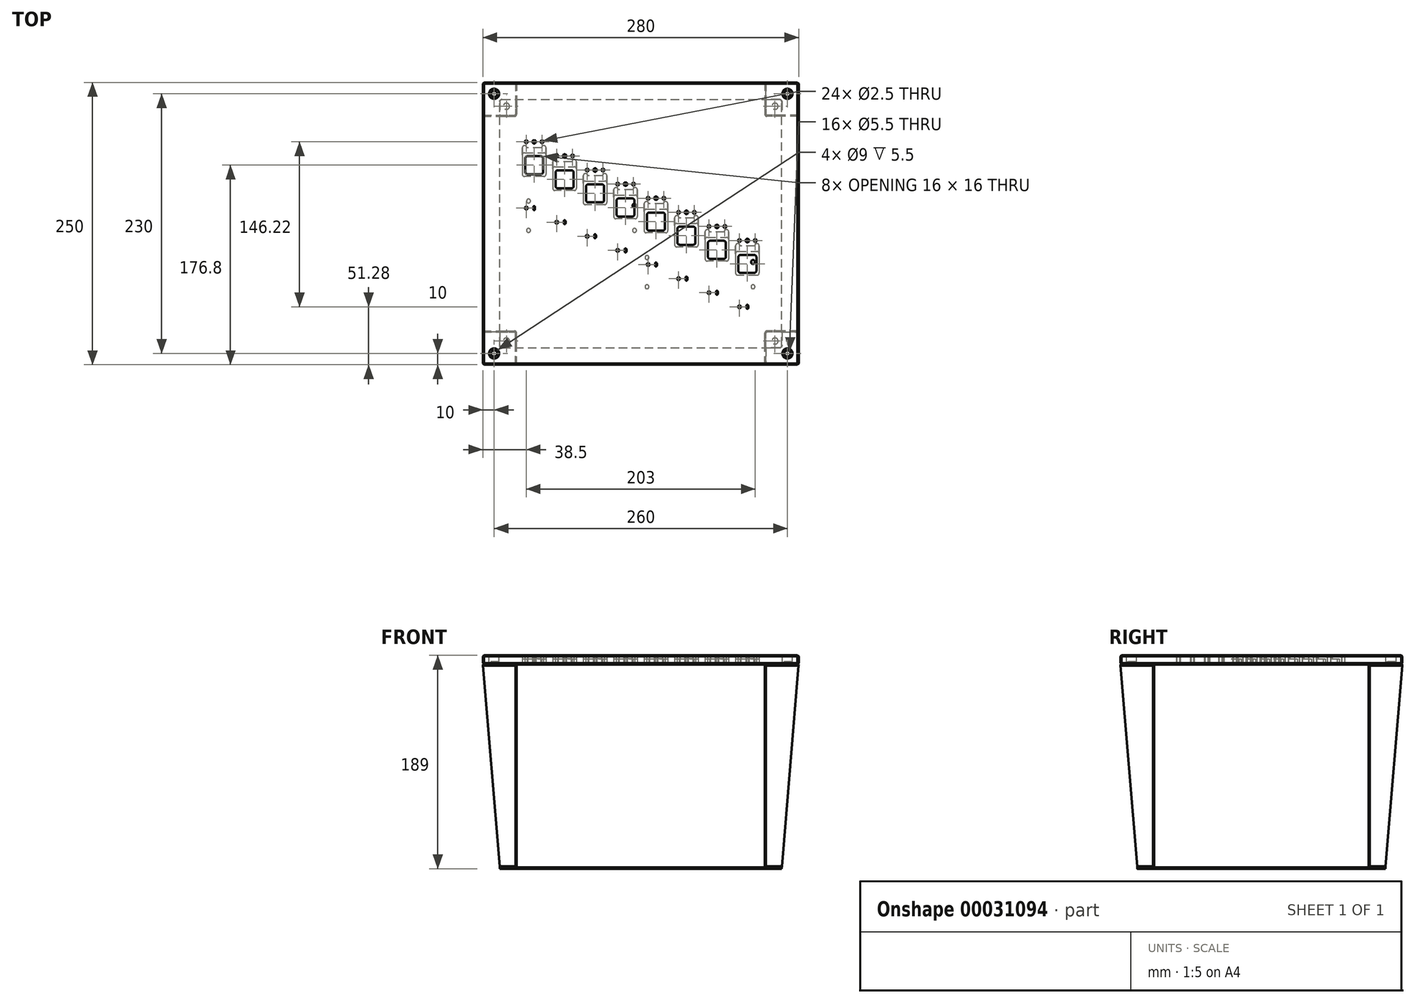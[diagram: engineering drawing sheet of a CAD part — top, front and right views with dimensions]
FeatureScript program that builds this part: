
annotation { "Feature Type Name" : "Feature", "Feature Type Description" : "" }
export const myFeature = defineFeature(function(context is Context, id is Id, definition is map)
    precondition{}
    {
        {
            var Q0;
            Q0=qCreatedBy(makeId("Top.planeOp"),FACE);
            var sketch = newSketch(context, id + "F0", { "sketchPlane" : qUnion([Q0])});
            skLineSegment(sketch, "E0", {"start": v(-94.5, 72.5) * mm, "end": v(-67.5, 60) * mm, "construction": true});
            skLineSegment(sketch, "E1", {"start": v(-67.5, 60) * mm, "end": v(-40.5, 47.5) * mm, "construction": true});
            skLineSegment(sketch, "E2", {"start": v(-40.5, 47.5) * mm, "end": v(-13.5, 35) * mm, "construction": true});
            skLineSegment(sketch, "E3", {"start": v(-13.5, 35) * mm, "end": v(13.5, 22.5) * mm, "construction": true});
            skLineSegment(sketch, "E4", {"start": v(13.5, 22.5) * mm, "end": v(40.5, 10) * mm, "construction": true});
            skLineSegment(sketch, "E5", {"start": v(40.5, 10) * mm, "end": v(67.5, -2.5) * mm, "construction": true});
            skLineSegment(sketch, "E6", {"start": v(67.5, -2.5) * mm, "end": v(94.5, -15) * mm, "construction": true});
            skLineSegment(sketch, "E7", {"start": v(-125, -110) * mm, "end": v(125, 110) * mm, "construction": true});
            skPoint(sketch, "E8", {"position": v(-125, 110) * mm});
            skPoint(sketch, "E9", {"position": v(125, 110) * mm});
            skPoint(sketch, "E10", {"position": v(125, -110) * mm});
            skPoint(sketch, "E11", {"position": v(-125, -110) * mm});
            skLineSegment(sketch, "E12", {"start": v(-125, 110) * mm, "end": v(125, 110) * mm, "construction": true});
            skLineSegment(sketch, "E13", {"start": v(125, 110) * mm, "end": v(125, -110) * mm, "construction": true});
            skLineSegment(sketch, "E14", {"start": v(125, -110) * mm, "end": v(-125, -110) * mm, "construction": true});
            skLineSegment(sketch, "E15", {"start": v(-125, -110) * mm, "end": v(-125, 110) * mm, "construction": true});
            skLineSegment(sketch, "E16", {"start": v(-94.5, 72.5) * mm, "end": v(-125, 72.5) * mm, "construction": true});
            skLineSegment(sketch, "E17", {"start": v(94.5, -15) * mm, "end": v(125, -15) * mm, "construction": true});
            skLineSegment(sketch, "E18", {"start": v(-94.5, 72.5) * mm, "end": v(-94.5, 110) * mm, "construction": true});
            skLineSegment(sketch, "E19", {"start": v(94.5, -15) * mm, "end": v(94.5, -110) * mm, "construction": true});
            skLineSegment(sketch, "E20.bottom", {"start": v(-140, 125) * mm, "end": v(140, 125) * mm});
            skLineSegment(sketch, "E20.top", {"start": v(-140, -125) * mm, "end": v(140, -125) * mm});
            skLineSegment(sketch, "E20.left", {"start": v(-140, 125) * mm, "end": v(-140, -125) * mm});
            skLineSegment(sketch, "E20.right", {"start": v(140, 125) * mm, "end": v(140, -125) * mm});
            skLineSegment(sketch, "E21", {"start": v(-47.5, 47.5) * mm, "end": v(-33.5, 47.5) * mm, "construction": true});
            skLineSegment(sketch, "E22", {"start": v(-40.5, 47.5) * mm, "end": v(-40.5, -11.22) * mm, "construction": true});
            skLineSegment(sketch, "E23", {"start": v(-40.5, -11.22) * mm, "end": v(-47.5, -11.22) * mm, "construction": true});
            skLineSegment(sketch, "E24.bottom", {"start": v(-46.5, 34.8) * mm, "end": v(-34.5, 34.8) * mm});
            skLineSegment(sketch, "E24.top", {"start": v(-46.5, 18.8) * mm, "end": v(-34.5, 18.8) * mm});
            skLineSegment(sketch, "E24.left", {"start": v(-48.5, 32.8) * mm, "end": v(-48.5, 20.8) * mm});
            skLineSegment(sketch, "E24.right", {"start": v(-32.5, 32.8) * mm, "end": v(-32.5, 20.8) * mm});
            skPoint(sketch, "E25.visualSharp", {"position": v(-48.5, 34.8) * mm});
            skArc(sketch, "E25.filletArc", {"start": v(-46.5, 34.8) * mm, "mid": v(-47.91, 34.21) * mm, "end": v(-48.5, 32.8) * mm});
            skPoint(sketch, "E26.visualSharp", {"position": v(-48.5, 18.8) * mm});
            skArc(sketch, "E26.filletArc", {"start": v(-48.5, 20.8) * mm, "mid": v(-47.91, 19.39) * mm, "end": v(-46.5, 18.8) * mm});
            skPoint(sketch, "E27.visualSharp", {"position": v(-32.5, 18.8) * mm});
            skArc(sketch, "E27.filletArc", {"start": v(-34.5, 18.8) * mm, "mid": v(-33.09, 19.39) * mm, "end": v(-32.5, 20.8) * mm});
            skPoint(sketch, "E28.visualSharp", {"position": v(-32.5, 34.8) * mm});
            skArc(sketch, "E28.filletArc", {"start": v(-32.5, 32.8) * mm, "mid": v(-33.09, 34.21) * mm, "end": v(-34.5, 34.8) * mm});
            skPoint(sketch, "E29", {"position": v(-40.5, 34.8) * mm});
            skLineSegment(sketch, "E30", {"start": v(-40.5, -10.22) * mm, "end": v(-40.5, -12.22) * mm});
            skArc(sketch, "E31.0.startCap", {"start": v(-41.27, -10.22) * mm, "mid": v(-40.5, -9.45) * mm, "end": v(-39.73, -10.22) * mm});
            skArc(sketch, "E31.0.endCap", {"start": v(-39.73, -12.22) * mm, "mid": v(-40.5, -12.98) * mm, "end": v(-41.27, -12.22) * mm});
            skLineSegment(sketch, "E31.0.left", {"start": v(-39.73, -10.22) * mm, "end": v(-39.73, -12.22) * mm});
            skLineSegment(sketch, "E31.0.right", {"start": v(-41.26, -10.22) * mm, "end": v(-41.26, -12.22) * mm});
            skCircle(sketch, "E32", {"center": v(-40.5, 47.5) * mm, "radius": 1.52 * mm});
            skCircle(sketch, "E33", {"center": v(-47.5, 47.5) * mm, "radius": 1.25 * mm});
            skCircle(sketch, "E34", {"center": v(-33.5, 47.5) * mm, "radius": 1.25 * mm});
            skCircle(sketch, "E35", {"center": v(-47.5, -11.22) * mm, "radius": 1.25 * mm});
            skPoint(sketch, "E36.visualSharp", {"position": v(-75.5, 31.3) * mm});
            skPoint(sketch, "E37.visualSharp", {"position": v(-59.5, 47.3) * mm});
            skPoint(sketch, "E38.visualSharp", {"position": v(-75.5, 47.3) * mm});
            skPoint(sketch, "E39.visualSharp", {"position": v(-59.5, 31.3) * mm});
            skLineSegment(sketch, "E40", {"start": v(-67.5, 60) * mm, "end": v(-67.5, 1.28) * mm, "construction": true});
            skPoint(sketch, "E41", {"position": v(-67.5, 47.3) * mm});
            skCircle(sketch, "E42", {"center": v(-67.5, 60) * mm, "radius": 1.52 * mm});
            skCircle(sketch, "E43", {"center": v(-74.5, 60) * mm, "radius": 1.25 * mm});
            skCircle(sketch, "E44", {"center": v(-74.5, 1.28) * mm, "radius": 1.25 * mm});
            skLineSegment(sketch, "E45", {"start": v(-67.5, 1.28) * mm, "end": v(-74.5, 1.28) * mm, "construction": true});
            skLineSegment(sketch, "E46", {"start": v(-74.5, 60) * mm, "end": v(-60.5, 60) * mm, "construction": true});
            skLineSegment(sketch, "E47.top", {"start": v(-73.5, 31.3) * mm, "end": v(-61.5, 31.3) * mm});
            skLineSegment(sketch, "E47.right", {"start": v(-59.5, 45.3) * mm, "end": v(-59.5, 33.3) * mm});
            skArc(sketch, "E39.filletArc", {"start": v(-61.5, 31.3) * mm, "mid": v(-60.09, 31.89) * mm, "end": v(-59.5, 33.3) * mm});
            skArc(sketch, "E38.filletArc", {"start": v(-73.5, 47.3) * mm, "mid": v(-74.91, 46.71) * mm, "end": v(-75.5, 45.3) * mm});
            skLineSegment(sketch, "E47.left", {"start": v(-75.5, 45.3) * mm, "end": v(-75.5, 33.3) * mm});
            skArc(sketch, "E36.filletArc", {"start": v(-75.5, 33.3) * mm, "mid": v(-74.91, 31.89) * mm, "end": v(-73.5, 31.3) * mm});
            skArc(sketch, "E37.filletArc", {"start": v(-59.5, 45.3) * mm, "mid": v(-60.09, 46.71) * mm, "end": v(-61.5, 47.3) * mm});
            skLineSegment(sketch, "E47.bottom", {"start": v(-73.5, 47.3) * mm, "end": v(-61.5, 47.3) * mm});
            skCircle(sketch, "E48", {"center": v(-60.5, 60) * mm, "radius": 1.25 * mm});
            skArc(sketch, "E49.0.endCap", {"start": v(-66.73, 0.28) * mm, "mid": v(-67.5, -0.48) * mm, "end": v(-68.26, 0.28) * mm});
            skArc(sketch, "E49.0.startCap", {"start": v(-68.26, 2.28) * mm, "mid": v(-67.5, 3.05) * mm, "end": v(-66.73, 2.28) * mm});
            skLineSegment(sketch, "E49.0.right", {"start": v(-68.26, 2.28) * mm, "end": v(-68.26, 0.28) * mm});
            skLineSegment(sketch, "E49.0.left", {"start": v(-66.73, 2.28) * mm, "end": v(-66.73, 0.28) * mm});
            skLineSegment(sketch, "E50", {"start": v(-67.5, 2.28) * mm, "end": v(-67.5, 0.28) * mm});
            skPoint(sketch, "E51.visualSharp", {"position": v(-102.5, 43.8) * mm});
            skPoint(sketch, "E52.visualSharp", {"position": v(-86.5, 59.8) * mm});
            skPoint(sketch, "E53.visualSharp", {"position": v(-102.5, 59.8) * mm});
            skPoint(sketch, "E54.visualSharp", {"position": v(-86.5, 43.8) * mm});
            skLineSegment(sketch, "E55", {"start": v(-94.5, 72.5) * mm, "end": v(-94.5, 13.78) * mm, "construction": true});
            skPoint(sketch, "E56", {"position": v(-94.5, 59.8) * mm});
            skCircle(sketch, "E57", {"center": v(-94.5, 72.5) * mm, "radius": 1.52 * mm});
            skCircle(sketch, "E58", {"center": v(-101.5, 72.5) * mm, "radius": 1.25 * mm});
            skCircle(sketch, "E59", {"center": v(-101.5, 13.78) * mm, "radius": 1.25 * mm});
            skLineSegment(sketch, "E60", {"start": v(-94.5, 13.78) * mm, "end": v(-101.5, 13.78) * mm, "construction": true});
            skLineSegment(sketch, "E61", {"start": v(-101.5, 72.5) * mm, "end": v(-87.5, 72.5) * mm, "construction": true});
            skLineSegment(sketch, "E62.top", {"start": v(-100.5, 43.8) * mm, "end": v(-88.5, 43.8) * mm});
            skLineSegment(sketch, "E62.right", {"start": v(-86.5, 57.8) * mm, "end": v(-86.5, 45.8) * mm});
            skArc(sketch, "E54.filletArc", {"start": v(-88.5, 43.8) * mm, "mid": v(-87.09, 44.39) * mm, "end": v(-86.5, 45.8) * mm});
            skArc(sketch, "E53.filletArc", {"start": v(-100.5, 59.8) * mm, "mid": v(-101.91, 59.21) * mm, "end": v(-102.5, 57.8) * mm});
            skLineSegment(sketch, "E62.left", {"start": v(-102.5, 57.8) * mm, "end": v(-102.5, 45.8) * mm});
            skArc(sketch, "E51.filletArc", {"start": v(-102.5, 45.8) * mm, "mid": v(-101.91, 44.39) * mm, "end": v(-100.5, 43.8) * mm});
            skArc(sketch, "E52.filletArc", {"start": v(-86.5, 57.8) * mm, "mid": v(-87.09, 59.21) * mm, "end": v(-88.5, 59.8) * mm});
            skLineSegment(sketch, "E62.bottom", {"start": v(-100.5, 59.8) * mm, "end": v(-88.5, 59.8) * mm});
            skCircle(sketch, "E63", {"center": v(-87.5, 72.5) * mm, "radius": 1.25 * mm});
            skArc(sketch, "E64.0.endCap", {"start": v(-93.73, 12.78) * mm, "mid": v(-94.5, 12.02) * mm, "end": v(-95.26, 12.78) * mm});
            skArc(sketch, "E64.0.startCap", {"start": v(-95.26, 14.78) * mm, "mid": v(-94.5, 15.55) * mm, "end": v(-93.73, 14.78) * mm});
            skLineSegment(sketch, "E64.0.right", {"start": v(-95.26, 14.78) * mm, "end": v(-95.26, 12.78) * mm});
            skLineSegment(sketch, "E64.0.left", {"start": v(-93.73, 14.78) * mm, "end": v(-93.73, 12.78) * mm});
            skLineSegment(sketch, "E65", {"start": v(-94.5, 14.78) * mm, "end": v(-94.5, 12.78) * mm});
            skPoint(sketch, "E66.visualSharp", {"position": v(-21.5, 6.3) * mm});
            skPoint(sketch, "E67.visualSharp", {"position": v(-5.5, 22.3) * mm});
            skPoint(sketch, "E68.visualSharp", {"position": v(-21.5, 22.3) * mm});
            skPoint(sketch, "E69.visualSharp", {"position": v(-5.5, 6.3) * mm});
            skLineSegment(sketch, "E70", {"start": v(-13.5, 35) * mm, "end": v(-13.5, -23.72) * mm, "construction": true});
            skPoint(sketch, "E71", {"position": v(-13.5, 22.3) * mm});
            skCircle(sketch, "E72", {"center": v(-13.5, 35) * mm, "radius": 1.52 * mm});
            skCircle(sketch, "E73", {"center": v(-20.5, 35) * mm, "radius": 1.25 * mm});
            skCircle(sketch, "E74", {"center": v(-20.5, -23.72) * mm, "radius": 1.25 * mm});
            skLineSegment(sketch, "E75", {"start": v(-13.5, -23.72) * mm, "end": v(-20.5, -23.72) * mm, "construction": true});
            skLineSegment(sketch, "E76", {"start": v(-20.5, 35) * mm, "end": v(-6.5, 35) * mm, "construction": true});
            skLineSegment(sketch, "E77.top", {"start": v(-19.5, 6.3) * mm, "end": v(-7.5, 6.3) * mm});
            skLineSegment(sketch, "E77.right", {"start": v(-5.5, 20.3) * mm, "end": v(-5.5, 8.3) * mm});
            skArc(sketch, "E69.filletArc", {"start": v(-7.5, 6.3) * mm, "mid": v(-6.09, 6.89) * mm, "end": v(-5.5, 8.3) * mm});
            skArc(sketch, "E68.filletArc", {"start": v(-19.5, 22.3) * mm, "mid": v(-20.91, 21.71) * mm, "end": v(-21.5, 20.3) * mm});
            skLineSegment(sketch, "E77.left", {"start": v(-21.5, 20.3) * mm, "end": v(-21.5, 8.3) * mm});
            skArc(sketch, "E66.filletArc", {"start": v(-21.5, 8.3) * mm, "mid": v(-20.91, 6.89) * mm, "end": v(-19.5, 6.3) * mm});
            skArc(sketch, "E67.filletArc", {"start": v(-5.5, 20.3) * mm, "mid": v(-6.09, 21.71) * mm, "end": v(-7.5, 22.3) * mm});
            skLineSegment(sketch, "E77.bottom", {"start": v(-19.5, 22.3) * mm, "end": v(-7.5, 22.3) * mm});
            skCircle(sketch, "E78", {"center": v(-6.5, 35) * mm, "radius": 1.25 * mm});
            skArc(sketch, "E79.0.endCap", {"start": v(-12.73, -24.72) * mm, "mid": v(-13.5, -25.48) * mm, "end": v(-14.27, -24.72) * mm});
            skArc(sketch, "E79.0.startCap", {"start": v(-14.27, -22.72) * mm, "mid": v(-13.5, -21.95) * mm, "end": v(-12.73, -22.72) * mm});
            skLineSegment(sketch, "E79.0.right", {"start": v(-14.26, -22.72) * mm, "end": v(-14.26, -24.72) * mm});
            skLineSegment(sketch, "E79.0.left", {"start": v(-12.73, -22.72) * mm, "end": v(-12.73, -24.72) * mm});
            skLineSegment(sketch, "E80", {"start": v(-13.5, -22.72) * mm, "end": v(-13.5, -24.72) * mm});
            skPoint(sketch, "E81.visualSharp", {"position": v(5.5, -6.2) * mm});
            skPoint(sketch, "E82.visualSharp", {"position": v(21.5, 9.8) * mm});
            skPoint(sketch, "E83.visualSharp", {"position": v(5.5, 9.8) * mm});
            skPoint(sketch, "E84.visualSharp", {"position": v(21.5, -6.2) * mm});
            skLineSegment(sketch, "E85", {"start": v(13.5, 22.5) * mm, "end": v(13.5, -36.22) * mm, "construction": true});
            skPoint(sketch, "E86", {"position": v(13.5, 9.8) * mm});
            skCircle(sketch, "E87", {"center": v(13.5, 22.5) * mm, "radius": 1.52 * mm});
            skCircle(sketch, "E88", {"center": v(6.5, 22.5) * mm, "radius": 1.25 * mm});
            skCircle(sketch, "E89", {"center": v(6.5, -36.22) * mm, "radius": 1.25 * mm});
            skLineSegment(sketch, "E90", {"start": v(13.5, -36.22) * mm, "end": v(6.5, -36.22) * mm, "construction": true});
            skLineSegment(sketch, "E91", {"start": v(6.5, 22.5) * mm, "end": v(20.5, 22.5) * mm, "construction": true});
            skLineSegment(sketch, "E92.top", {"start": v(7.5, -6.2) * mm, "end": v(19.5, -6.2) * mm});
            skLineSegment(sketch, "E92.right", {"start": v(21.5, 7.8) * mm, "end": v(21.5, -4.2) * mm});
            skArc(sketch, "E84.filletArc", {"start": v(19.5, -6.2) * mm, "mid": v(20.91, -5.61) * mm, "end": v(21.5, -4.2) * mm});
            skArc(sketch, "E83.filletArc", {"start": v(7.5, 9.8) * mm, "mid": v(6.09, 9.21) * mm, "end": v(5.5, 7.8) * mm});
            skLineSegment(sketch, "E92.left", {"start": v(5.5, 7.8) * mm, "end": v(5.5, -4.2) * mm});
            skArc(sketch, "E81.filletArc", {"start": v(5.5, -4.2) * mm, "mid": v(6.09, -5.61) * mm, "end": v(7.5, -6.2) * mm});
            skArc(sketch, "E82.filletArc", {"start": v(21.5, 7.8) * mm, "mid": v(20.91, 9.21) * mm, "end": v(19.5, 9.8) * mm});
            skLineSegment(sketch, "E92.bottom", {"start": v(7.5, 9.8) * mm, "end": v(19.5, 9.8) * mm});
            skCircle(sketch, "E93", {"center": v(20.5, 22.5) * mm, "radius": 1.25 * mm});
            skArc(sketch, "E94.0.endCap", {"start": v(14.27, -37.22) * mm, "mid": v(13.5, -37.98) * mm, "end": v(12.74, -37.22) * mm});
            skArc(sketch, "E94.0.startCap", {"start": v(12.74, -35.22) * mm, "mid": v(13.5, -34.45) * mm, "end": v(14.27, -35.22) * mm});
            skLineSegment(sketch, "E94.0.right", {"start": v(12.74, -35.22) * mm, "end": v(12.74, -37.22) * mm});
            skLineSegment(sketch, "E94.0.left", {"start": v(14.27, -35.22) * mm, "end": v(14.27, -37.22) * mm});
            skLineSegment(sketch, "E95", {"start": v(13.5, -35.22) * mm, "end": v(13.5, -37.22) * mm});
            skPoint(sketch, "E96.visualSharp", {"position": v(32.5, -18.7) * mm});
            skPoint(sketch, "E97.visualSharp", {"position": v(48.5, -2.7) * mm});
            skPoint(sketch, "E98.visualSharp", {"position": v(32.5, -2.7) * mm});
            skPoint(sketch, "E99.visualSharp", {"position": v(48.5, -18.7) * mm});
            skLineSegment(sketch, "E100", {"start": v(40.5, 10) * mm, "end": v(40.5, -48.72) * mm, "construction": true});
            skPoint(sketch, "E101", {"position": v(40.5, -2.7) * mm});
            skCircle(sketch, "E102", {"center": v(40.5, 10) * mm, "radius": 1.52 * mm});
            skCircle(sketch, "E103", {"center": v(33.5, 10) * mm, "radius": 1.25 * mm});
            skCircle(sketch, "E104", {"center": v(33.5, -48.72) * mm, "radius": 1.25 * mm});
            skLineSegment(sketch, "E105", {"start": v(40.5, -48.72) * mm, "end": v(33.5, -48.72) * mm, "construction": true});
            skLineSegment(sketch, "E106", {"start": v(33.5, 10) * mm, "end": v(47.5, 10) * mm, "construction": true});
            skLineSegment(sketch, "E107.top", {"start": v(34.5, -18.7) * mm, "end": v(46.5, -18.7) * mm});
            skLineSegment(sketch, "E107.right", {"start": v(48.5, -4.7) * mm, "end": v(48.5, -16.7) * mm});
            skArc(sketch, "E99.filletArc", {"start": v(46.5, -18.7) * mm, "mid": v(47.91, -18.11) * mm, "end": v(48.5, -16.7) * mm});
            skArc(sketch, "E98.filletArc", {"start": v(34.5, -2.7) * mm, "mid": v(33.09, -3.29) * mm, "end": v(32.5, -4.7) * mm});
            skLineSegment(sketch, "E107.left", {"start": v(32.5, -4.7) * mm, "end": v(32.5, -16.7) * mm});
            skArc(sketch, "E96.filletArc", {"start": v(32.5, -16.7) * mm, "mid": v(33.09, -18.11) * mm, "end": v(34.5, -18.7) * mm});
            skArc(sketch, "E97.filletArc", {"start": v(48.5, -4.7) * mm, "mid": v(47.91, -3.29) * mm, "end": v(46.5, -2.7) * mm});
            skLineSegment(sketch, "E107.bottom", {"start": v(34.5, -2.7) * mm, "end": v(46.5, -2.7) * mm});
            skCircle(sketch, "E108", {"center": v(47.5, 10) * mm, "radius": 1.25 * mm});
            skArc(sketch, "E109.0.endCap", {"start": v(41.27, -49.72) * mm, "mid": v(40.5, -50.48) * mm, "end": v(39.73, -49.72) * mm});
            skArc(sketch, "E109.0.startCap", {"start": v(39.73, -47.72) * mm, "mid": v(40.5, -46.95) * mm, "end": v(41.27, -47.72) * mm});
            skLineSegment(sketch, "E109.0.right", {"start": v(39.73, -47.72) * mm, "end": v(39.73, -49.72) * mm});
            skLineSegment(sketch, "E109.0.left", {"start": v(41.26, -47.72) * mm, "end": v(41.26, -49.72) * mm});
            skLineSegment(sketch, "E110", {"start": v(40.5, -47.72) * mm, "end": v(40.5, -49.72) * mm});
            skPoint(sketch, "E111.visualSharp", {"position": v(59.5, -31.2) * mm});
            skPoint(sketch, "E112.visualSharp", {"position": v(75.5, -15.2) * mm});
            skPoint(sketch, "E113.visualSharp", {"position": v(59.5, -15.2) * mm});
            skPoint(sketch, "E114.visualSharp", {"position": v(75.5, -31.2) * mm});
            skLineSegment(sketch, "E115", {"start": v(67.5, -2.5) * mm, "end": v(67.5, -61.22) * mm, "construction": true});
            skPoint(sketch, "E116", {"position": v(67.5, -15.2) * mm});
            skCircle(sketch, "E117", {"center": v(67.5, -2.5) * mm, "radius": 1.52 * mm});
            skCircle(sketch, "E118", {"center": v(60.5, -2.5) * mm, "radius": 1.25 * mm});
            skCircle(sketch, "E119", {"center": v(60.5, -61.22) * mm, "radius": 1.25 * mm});
            skLineSegment(sketch, "E120", {"start": v(67.5, -61.22) * mm, "end": v(60.5, -61.22) * mm, "construction": true});
            skLineSegment(sketch, "E121", {"start": v(60.5, -2.5) * mm, "end": v(74.5, -2.5) * mm, "construction": true});
            skLineSegment(sketch, "E122.top", {"start": v(61.5, -31.2) * mm, "end": v(73.5, -31.2) * mm});
            skLineSegment(sketch, "E122.right", {"start": v(75.5, -17.2) * mm, "end": v(75.5, -29.2) * mm});
            skArc(sketch, "E114.filletArc", {"start": v(73.5, -31.2) * mm, "mid": v(74.91, -30.61) * mm, "end": v(75.5, -29.2) * mm});
            skArc(sketch, "E113.filletArc", {"start": v(61.5, -15.2) * mm, "mid": v(60.09, -15.79) * mm, "end": v(59.5, -17.2) * mm});
            skLineSegment(sketch, "E122.left", {"start": v(59.5, -17.2) * mm, "end": v(59.5, -29.2) * mm});
            skArc(sketch, "E111.filletArc", {"start": v(59.5, -29.2) * mm, "mid": v(60.09, -30.61) * mm, "end": v(61.5, -31.2) * mm});
            skArc(sketch, "E112.filletArc", {"start": v(75.5, -17.2) * mm, "mid": v(74.91, -15.79) * mm, "end": v(73.5, -15.2) * mm});
            skLineSegment(sketch, "E122.bottom", {"start": v(61.5, -15.2) * mm, "end": v(73.5, -15.2) * mm});
            skCircle(sketch, "E123", {"center": v(74.5, -2.5) * mm, "radius": 1.25 * mm});
            skArc(sketch, "E124.0.endCap", {"start": v(68.26, -62.22) * mm, "mid": v(67.5, -62.98) * mm, "end": v(66.73, -62.22) * mm});
            skArc(sketch, "E124.0.startCap", {"start": v(66.73, -60.22) * mm, "mid": v(67.5, -59.45) * mm, "end": v(68.26, -60.22) * mm});
            skLineSegment(sketch, "E124.0.right", {"start": v(66.73, -60.22) * mm, "end": v(66.73, -62.22) * mm});
            skLineSegment(sketch, "E124.0.left", {"start": v(68.26, -60.22) * mm, "end": v(68.26, -62.22) * mm});
            skLineSegment(sketch, "E125", {"start": v(67.5, -60.22) * mm, "end": v(67.5, -62.22) * mm});
            skPoint(sketch, "E126.visualSharp", {"position": v(86.5, -43.7) * mm});
            skPoint(sketch, "E127.visualSharp", {"position": v(102.5, -27.7) * mm});
            skPoint(sketch, "E128.visualSharp", {"position": v(86.5, -27.7) * mm});
            skPoint(sketch, "E129.visualSharp", {"position": v(102.5, -43.7) * mm});
            skLineSegment(sketch, "E130", {"start": v(94.5, -15) * mm, "end": v(94.5, -73.72) * mm, "construction": true});
            skPoint(sketch, "E131", {"position": v(94.5, -27.7) * mm});
            skCircle(sketch, "E132", {"center": v(94.5, -15) * mm, "radius": 1.52 * mm});
            skCircle(sketch, "E133", {"center": v(87.5, -15) * mm, "radius": 1.25 * mm});
            skCircle(sketch, "E134", {"center": v(87.5, -73.72) * mm, "radius": 1.25 * mm});
            skLineSegment(sketch, "E135", {"start": v(94.5, -73.72) * mm, "end": v(87.5, -73.72) * mm, "construction": true});
            skLineSegment(sketch, "E136", {"start": v(87.5, -15) * mm, "end": v(101.5, -15) * mm, "construction": true});
            skLineSegment(sketch, "E137.top", {"start": v(88.5, -43.7) * mm, "end": v(100.5, -43.7) * mm});
            skLineSegment(sketch, "E137.right", {"start": v(102.5, -29.7) * mm, "end": v(102.5, -41.7) * mm});
            skArc(sketch, "E129.filletArc", {"start": v(100.5, -43.7) * mm, "mid": v(101.91, -43.11) * mm, "end": v(102.5, -41.7) * mm});
            skArc(sketch, "E128.filletArc", {"start": v(88.5, -27.7) * mm, "mid": v(87.09, -28.29) * mm, "end": v(86.5, -29.7) * mm});
            skLineSegment(sketch, "E137.left", {"start": v(86.5, -29.7) * mm, "end": v(86.5, -41.7) * mm});
            skArc(sketch, "E126.filletArc", {"start": v(86.5, -41.7) * mm, "mid": v(87.09, -43.11) * mm, "end": v(88.5, -43.7) * mm});
            skArc(sketch, "E127.filletArc", {"start": v(102.5, -29.7) * mm, "mid": v(101.91, -28.29) * mm, "end": v(100.5, -27.7) * mm});
            skLineSegment(sketch, "E137.bottom", {"start": v(88.5, -27.7) * mm, "end": v(100.5, -27.7) * mm});
            skCircle(sketch, "E138", {"center": v(101.5, -15) * mm, "radius": 1.25 * mm});
            skArc(sketch, "E139.0.endCap", {"start": v(95.27, -74.72) * mm, "mid": v(94.5, -75.49) * mm, "end": v(93.73, -74.72) * mm});
            skArc(sketch, "E139.0.startCap", {"start": v(93.73, -72.72) * mm, "mid": v(94.5, -71.96) * mm, "end": v(95.27, -72.72) * mm});
            skLineSegment(sketch, "E139.0.right", {"start": v(93.73, -72.72) * mm, "end": v(93.73, -74.72) * mm});
            skLineSegment(sketch, "E139.0.left", {"start": v(95.26, -72.72) * mm, "end": v(95.26, -74.72) * mm});
            skLineSegment(sketch, "E140", {"start": v(94.5, -72.72) * mm, "end": v(94.5, -74.72) * mm});
            skSolve(sketch);
        }
        {
            var Q0;
            Q0 = qSketchRegion(id + "F0", true);
            extrude(context, id + "F1", {"entities" : qUnion([Q0]), "depth" : 8 * mm});
        }
        {
            var Q0;
            Q0=makeQuery(id+"F1.opExtrude","CAP_FACE",FACE,{"disambiguationData":[OSD([sQuery(id+"F0.wireOp",EDGE,"E20.bottom"),sQuery(id+"F0.wireOp",EDGE,"E20.top"),sQuery(id+"F0.wireOp",EDGE,"E20.left"),sQuery(id+"F0.wireOp",EDGE,"E20.right"),sQuery(id+"F0.wireOp",EDGE,"E24.bottom"),sQuery(id+"F0.wireOp",EDGE,"E24.top"),sQuery(id+"F0.wireOp",EDGE,"E24.left"),sQuery(id+"F0.wireOp",EDGE,"E24.right"),sQuery(id+"F0.wireOp",EDGE,"E25.filletArc"),sQuery(id+"F0.wireOp",EDGE,"E26.filletArc"),sQuery(id+"F0.wireOp",EDGE,"E27.filletArc"),sQuery(id+"F0.wireOp",EDGE,"E28.filletArc"),sQuery(id+"F0.wireOp",EDGE,"E31.0.startCap"),sQuery(id+"F0.wireOp",EDGE,"E31.0.endCap"),sQuery(id+"F0.wireOp",EDGE,"E31.0.left"),sQuery(id+"F0.wireOp",EDGE,"E31.0.right"),sQuery(id+"F0.wireOp",EDGE,"E32"),sQuery(id+"F0.wireOp",EDGE,"E33"),sQuery(id+"F0.wireOp",EDGE,"E34"),sQuery(id+"F0.wireOp",EDGE,"E35"),sQuery(id+"F0.wireOp",EDGE,"E42"),sQuery(id+"F0.wireOp",EDGE,"E43"),sQuery(id+"F0.wireOp",EDGE,"E44"),sQuery(id+"F0.wireOp",EDGE,"E47.top"),sQuery(id+"F0.wireOp",EDGE,"E47.right"),sQuery(id+"F0.wireOp",EDGE,"E39.filletArc"),sQuery(id+"F0.wireOp",EDGE,"E38.filletArc"),sQuery(id+"F0.wireOp",EDGE,"E47.left"),sQuery(id+"F0.wireOp",EDGE,"E36.filletArc"),sQuery(id+"F0.wireOp",EDGE,"E37.filletArc"),sQuery(id+"F0.wireOp",EDGE,"E47.bottom"),sQuery(id+"F0.wireOp",EDGE,"E48"),sQuery(id+"F0.wireOp",EDGE,"E49.0.endCap"),sQuery(id+"F0.wireOp",EDGE,"E49.0.startCap"),sQuery(id+"F0.wireOp",EDGE,"E49.0.right"),sQuery(id+"F0.wireOp",EDGE,"E49.0.left"),sQuery(id+"F0.wireOp",EDGE,"E57"),sQuery(id+"F0.wireOp",EDGE,"E58"),sQuery(id+"F0.wireOp",EDGE,"E59"),sQuery(id+"F0.wireOp",EDGE,"E62.top"),sQuery(id+"F0.wireOp",EDGE,"E62.right"),sQuery(id+"F0.wireOp",EDGE,"E54.filletArc"),sQuery(id+"F0.wireOp",EDGE,"E53.filletArc"),sQuery(id+"F0.wireOp",EDGE,"E62.left"),sQuery(id+"F0.wireOp",EDGE,"E51.filletArc"),sQuery(id+"F0.wireOp",EDGE,"E52.filletArc"),sQuery(id+"F0.wireOp",EDGE,"E62.bottom"),sQuery(id+"F0.wireOp",EDGE,"E63"),sQuery(id+"F0.wireOp",EDGE,"E64.0.endCap"),sQuery(id+"F0.wireOp",EDGE,"E64.0.startCap"),sQuery(id+"F0.wireOp",EDGE,"E64.0.right"),sQuery(id+"F0.wireOp",EDGE,"E64.0.left"),sQuery(id+"F0.wireOp",EDGE,"E72"),sQuery(id+"F0.wireOp",EDGE,"E73"),sQuery(id+"F0.wireOp",EDGE,"E74"),sQuery(id+"F0.wireOp",EDGE,"E77.top"),sQuery(id+"F0.wireOp",EDGE,"E77.right"),sQuery(id+"F0.wireOp",EDGE,"E69.filletArc"),sQuery(id+"F0.wireOp",EDGE,"E68.filletArc"),sQuery(id+"F0.wireOp",EDGE,"E77.left"),sQuery(id+"F0.wireOp",EDGE,"E66.filletArc"),sQuery(id+"F0.wireOp",EDGE,"E67.filletArc"),sQuery(id+"F0.wireOp",EDGE,"E77.bottom"),sQuery(id+"F0.wireOp",EDGE,"E78"),sQuery(id+"F0.wireOp",EDGE,"E79.0.endCap"),sQuery(id+"F0.wireOp",EDGE,"E79.0.startCap"),sQuery(id+"F0.wireOp",EDGE,"E79.0.right"),sQuery(id+"F0.wireOp",EDGE,"E79.0.left"),sQuery(id+"F0.wireOp",EDGE,"E87"),sQuery(id+"F0.wireOp",EDGE,"E88"),sQuery(id+"F0.wireOp",EDGE,"E89"),sQuery(id+"F0.wireOp",EDGE,"E92.top"),sQuery(id+"F0.wireOp",EDGE,"E92.right"),sQuery(id+"F0.wireOp",EDGE,"E84.filletArc"),sQuery(id+"F0.wireOp",EDGE,"E83.filletArc"),sQuery(id+"F0.wireOp",EDGE,"E92.left"),sQuery(id+"F0.wireOp",EDGE,"E81.filletArc"),sQuery(id+"F0.wireOp",EDGE,"E82.filletArc"),sQuery(id+"F0.wireOp",EDGE,"E92.bottom"),sQuery(id+"F0.wireOp",EDGE,"E93"),sQuery(id+"F0.wireOp",EDGE,"E94.0.endCap"),sQuery(id+"F0.wireOp",EDGE,"E94.0.startCap"),sQuery(id+"F0.wireOp",EDGE,"E94.0.right"),sQuery(id+"F0.wireOp",EDGE,"E94.0.left"),sQuery(id+"F0.wireOp",EDGE,"E102"),sQuery(id+"F0.wireOp",EDGE,"E103"),sQuery(id+"F0.wireOp",EDGE,"E104"),sQuery(id+"F0.wireOp",EDGE,"E107.top"),sQuery(id+"F0.wireOp",EDGE,"E107.right"),sQuery(id+"F0.wireOp",EDGE,"E99.filletArc"),sQuery(id+"F0.wireOp",EDGE,"E98.filletArc"),sQuery(id+"F0.wireOp",EDGE,"E107.left"),sQuery(id+"F0.wireOp",EDGE,"E96.filletArc"),sQuery(id+"F0.wireOp",EDGE,"E97.filletArc"),sQuery(id+"F0.wireOp",EDGE,"E107.bottom"),sQuery(id+"F0.wireOp",EDGE,"E108"),sQuery(id+"F0.wireOp",EDGE,"E109.0.endCap"),sQuery(id+"F0.wireOp",EDGE,"E109.0.startCap"),sQuery(id+"F0.wireOp",EDGE,"E109.0.right"),sQuery(id+"F0.wireOp",EDGE,"E109.0.left"),sQuery(id+"F0.wireOp",EDGE,"E117"),sQuery(id+"F0.wireOp",EDGE,"E118"),sQuery(id+"F0.wireOp",EDGE,"E119"),sQuery(id+"F0.wireOp",EDGE,"E122.top"),sQuery(id+"F0.wireOp",EDGE,"E122.right"),sQuery(id+"F0.wireOp",EDGE,"E114.filletArc"),sQuery(id+"F0.wireOp",EDGE,"E113.filletArc"),sQuery(id+"F0.wireOp",EDGE,"E122.left"),sQuery(id+"F0.wireOp",EDGE,"E111.filletArc"),sQuery(id+"F0.wireOp",EDGE,"E112.filletArc"),sQuery(id+"F0.wireOp",EDGE,"E122.bottom"),sQuery(id+"F0.wireOp",EDGE,"E123"),sQuery(id+"F0.wireOp",EDGE,"E124.0.endCap"),sQuery(id+"F0.wireOp",EDGE,"E124.0.startCap"),sQuery(id+"F0.wireOp",EDGE,"E124.0.right"),sQuery(id+"F0.wireOp",EDGE,"E124.0.left"),sQuery(id+"F0.wireOp",EDGE,"E132"),sQuery(id+"F0.wireOp",EDGE,"E133"),sQuery(id+"F0.wireOp",EDGE,"E134"),sQuery(id+"F0.wireOp",EDGE,"E137.top"),sQuery(id+"F0.wireOp",EDGE,"E137.right"),sQuery(id+"F0.wireOp",EDGE,"E129.filletArc"),sQuery(id+"F0.wireOp",EDGE,"E128.filletArc"),sQuery(id+"F0.wireOp",EDGE,"E137.left"),sQuery(id+"F0.wireOp",EDGE,"E126.filletArc"),sQuery(id+"F0.wireOp",EDGE,"E127.filletArc"),sQuery(id+"F0.wireOp",EDGE,"E137.bottom"),sQuery(id+"F0.wireOp",EDGE,"E138"),sQuery(id+"F0.wireOp",EDGE,"E139.0.endCap"),sQuery(id+"F0.wireOp",EDGE,"E139.0.startCap"),sQuery(id+"F0.wireOp",EDGE,"E139.0.right"),sQuery(id+"F0.wireOp",EDGE,"E139.0.left")])],"isStart":true});
            var sketch = newSketch(context, id + "F2", { "sketchPlane" : qUnion([Q0])});
            skLineSegment(sketch, "E141.bottom", {"start": v(-140, 125) * mm, "end": v(-110, 125) * mm});
            skLineSegment(sketch, "E141.top", {"start": v(-140, 95) * mm, "end": v(-110, 95) * mm});
            skLineSegment(sketch, "E141.left", {"start": v(-140, 125) * mm, "end": v(-140, 95) * mm});
            skLineSegment(sketch, "E141.right", {"start": v(-110, 125) * mm, "end": v(-110, 95) * mm});
            skLineSegment(sketch, "E142.bottom", {"start": v(140, 125) * mm, "end": v(110, 125) * mm});
            skLineSegment(sketch, "E142.top", {"start": v(140, 95) * mm, "end": v(110, 95) * mm});
            skLineSegment(sketch, "E142.left", {"start": v(140, 125) * mm, "end": v(140, 95) * mm});
            skLineSegment(sketch, "E142.right", {"start": v(110, 125) * mm, "end": v(110, 95) * mm});
            skLineSegment(sketch, "E143.bottom", {"start": v(140, -125) * mm, "end": v(110, -125) * mm});
            skLineSegment(sketch, "E143.top", {"start": v(140, -95) * mm, "end": v(110, -95) * mm});
            skLineSegment(sketch, "E143.left", {"start": v(140, -125) * mm, "end": v(140, -95) * mm});
            skLineSegment(sketch, "E143.right", {"start": v(110, -125) * mm, "end": v(110, -95) * mm});
            skLineSegment(sketch, "E144.bottom", {"start": v(-140, -125) * mm, "end": v(-110, -125) * mm});
            skLineSegment(sketch, "E144.top", {"start": v(-140, -95) * mm, "end": v(-110, -95) * mm});
            skLineSegment(sketch, "E144.left", {"start": v(-140, -125) * mm, "end": v(-140, -95) * mm});
            skLineSegment(sketch, "E144.right", {"start": v(-110, -125) * mm, "end": v(-110, -95) * mm});
            skSolve(sketch);
        }
        {
            var Q0;
            {var subQ7=sQuery(id+"F2.wireOp",EDGE,"E141.top");Q0=makeQuery(id+"F2.imprint","IMPRINT",FACE,{"disambiguationData":[TD([[makeQuery(id+"F2.imprint","IMPRINT",EDGE,{"derivedFrom":subQ7}),-1.0]])]});}
            cPlane(context, id + "F3", {"entities" : qUnion([Q0]), "cplaneType" : CPlaneType.OFFSET, "offset" : 180 * mm, "width" : 150 * mm, "height" : 150 * mm});
        }
        {
            var Q0;
            Q0=qCreatedBy(id+"F3.planeOp",FACE);
            var sketch = newSketch(context, id + "F4", { "sketchPlane" : qUnion([Q0])});
            skLineSegment(sketch, "E145.bottom", {"start": v(-125, 110) * mm, "end": v(-110, 110) * mm});
            skLineSegment(sketch, "E145.top", {"start": v(-125, 95) * mm, "end": v(-110, 95) * mm});
            skLineSegment(sketch, "E145.left", {"start": v(-125, 110) * mm, "end": v(-125, 95) * mm});
            skLineSegment(sketch, "E145.right", {"start": v(-110, 110) * mm, "end": v(-110, 95) * mm});
            skLineSegment(sketch, "E146.bottom", {"start": v(125, 110) * mm, "end": v(110, 110) * mm});
            skLineSegment(sketch, "E146.top", {"start": v(125, 95) * mm, "end": v(110, 95) * mm});
            skLineSegment(sketch, "E146.left", {"start": v(125, 110) * mm, "end": v(125, 95) * mm});
            skLineSegment(sketch, "E146.right", {"start": v(110, 110) * mm, "end": v(110, 95) * mm});
            skLineSegment(sketch, "E147.bottom", {"start": v(125, -110) * mm, "end": v(110, -110) * mm});
            skLineSegment(sketch, "E147.top", {"start": v(125, -95) * mm, "end": v(110, -95) * mm});
            skLineSegment(sketch, "E147.left", {"start": v(125, -110) * mm, "end": v(125, -95) * mm});
            skLineSegment(sketch, "E147.right", {"start": v(110, -110) * mm, "end": v(110, -95) * mm});
            skLineSegment(sketch, "E148.bottom", {"start": v(-125, -110) * mm, "end": v(-110, -110) * mm});
            skLineSegment(sketch, "E148.top", {"start": v(-125, -95) * mm, "end": v(-110, -95) * mm});
            skLineSegment(sketch, "E148.left", {"start": v(-125, -110) * mm, "end": v(-125, -95) * mm});
            skLineSegment(sketch, "E148.right", {"start": v(-110, -110) * mm, "end": v(-110, -95) * mm});
            skSolve(sketch);
        }
        {
            var Q1;
            Q1=makeQuery(id+"F2.imprint","IMPRINT",FACE,{"disambiguationData":[TD([[makeQuery(id+"F2.imprint","IMPRINT",EDGE,{"derivedFrom":sQuery(id+"F2.wireOp",EDGE,"E141.bottom")}),-1.0]])]});
            var Q2;
            Q2=makeQuery(id+"F4.imprint","IMPRINT",FACE,{"disambiguationData":[TD([[makeQuery(id+"F4.imprint","IMPRINT",EDGE,{"derivedFrom":sQuery(id+"F4.wireOp",EDGE,"E145.bottom")}),-1.0]])]});
            loft(context, id + "F5", {"sheetProfilesArray" : [{ "sheetProfileEntities" : qUnion([Q1]) }, { "sheetProfileEntities" : qUnion([Q2]) }]});
        }
        {
            var Q0;
            Q0=makeQuery(id+"F2.imprint","IMPRINT",FACE,{"disambiguationData":[TD([[makeQuery(id+"F2.imprint","IMPRINT",EDGE,{"derivedFrom":sQuery(id+"F2.wireOp",EDGE,"E142.bottom")}),-1.0]])]});
            var Q1;
            Q1=makeQuery(id+"F4.imprint","IMPRINT",FACE,{"disambiguationData":[TD([[makeQuery(id+"F4.imprint","IMPRINT",EDGE,{"derivedFrom":sQuery(id+"F4.wireOp",EDGE,"E146.bottom")}),1.0]])]});
            loft(context, id + "F6", {"sheetProfilesArray" : [{ "sheetProfileEntities" : qUnion([Q0]) }, { "sheetProfileEntities" : qUnion([Q1]) }]});
        }
        {
            var Q1;
            Q1=makeQuery(id+"F2.imprint","IMPRINT",FACE,{"disambiguationData":[TD([[makeQuery(id+"F2.imprint","IMPRINT",EDGE,{"derivedFrom":sQuery(id+"F2.wireOp",EDGE,"E144.bottom")}),1.0]])]});
            var Q2;
            Q2=makeQuery(id+"F4.imprint","IMPRINT",FACE,{"disambiguationData":[TD([[makeQuery(id+"F4.imprint","IMPRINT",EDGE,{"derivedFrom":sQuery(id+"F4.wireOp",EDGE,"E148.bottom")}),1.0]])]});
            loft(context, id + "F7", {"sheetProfilesArray" : [{ "sheetProfileEntities" : qUnion([Q1]) }, { "sheetProfileEntities" : qUnion([Q2]) }]});
        }
        {
            var Q1;
            Q1=makeQuery(id+"F2.imprint","IMPRINT",FACE,{"disambiguationData":[TD([[makeQuery(id+"F2.imprint","IMPRINT",EDGE,{"derivedFrom":sQuery(id+"F2.wireOp",EDGE,"E143.bottom")}),1.0]])]});
            var Q2;
            Q2=makeQuery(id+"F4.imprint","IMPRINT",FACE,{"disambiguationData":[TD([[makeQuery(id+"F4.imprint","IMPRINT",EDGE,{"derivedFrom":sQuery(id+"F4.wireOp",EDGE,"E147.bottom")}),-1.0]])]});
            loft(context, id + "F8", {"sheetProfilesArray" : [{ "sheetProfileEntities" : qUnion([Q1]) }, { "sheetProfileEntities" : qUnion([Q2]) }]});
        }
        {
            var Q0;
            Q0=makeQuery(id+"F5.opLoft","SWEPT_FACE",FACE,{"disambiguationData":[OSD([sQuery(id+"F0.wireOp",EDGE,"E20.left"),sQuery(id+"F2.wireOp",EDGE,"E141.bottom"),sQuery(id+"F2.wireOp",EDGE,"E141.top"),sQuery(id+"F2.wireOp",EDGE,"E141.left"),sQuery(id+"F4.wireOp",EDGE,"E145.bottom"),sQuery(id+"F4.wireOp",EDGE,"E145.top"),sQuery(id+"F4.wireOp",EDGE,"E145.left")])]});
            var Q1;
            Q1=makeQuery(id+"F5.opLoft","SWEPT_FACE",FACE,{"disambiguationData":[OSD([sQuery(id+"F0.wireOp",EDGE,"E20.left"),sQuery(id+"F2.wireOp",EDGE,"E141.bottom"),sQuery(id+"F2.wireOp",EDGE,"E141.top"),sQuery(id+"F2.wireOp",EDGE,"E141.left"),sQuery(id+"F4.wireOp",EDGE,"E145.bottom"),sQuery(id+"F4.wireOp",EDGE,"E145.top"),sQuery(id+"F4.wireOp",EDGE,"E145.left")])]});
            var Q2;
            Q2=makeQuery(id+"F5.opLoft","SWEPT_FACE",FACE,{"disambiguationData":[OSD([sQuery(id+"F0.wireOp",EDGE,"E20.top"),sQuery(id+"F2.wireOp",EDGE,"E141.bottom"),sQuery(id+"F2.wireOp",EDGE,"E141.left"),sQuery(id+"F2.wireOp",EDGE,"E141.right"),sQuery(id+"F4.wireOp",EDGE,"E145.bottom"),sQuery(id+"F4.wireOp",EDGE,"E145.left"),sQuery(id+"F4.wireOp",EDGE,"E145.right")])]});
            var Q3;
            Q3=makeQuery(id+"F6.opLoft","SWEPT_FACE",FACE,{"disambiguationData":[OSD([sQuery(id+"F0.wireOp",EDGE,"E20.right"),sQuery(id+"F2.wireOp",EDGE,"E142.bottom"),sQuery(id+"F2.wireOp",EDGE,"E142.top"),sQuery(id+"F2.wireOp",EDGE,"E142.left"),sQuery(id+"F4.wireOp",EDGE,"E146.bottom"),sQuery(id+"F4.wireOp",EDGE,"E146.top"),sQuery(id+"F4.wireOp",EDGE,"E146.left")])]});
            var Q4;
            Q4=makeQuery(id+"F6.opLoft","SWEPT_FACE",FACE,{"disambiguationData":[OSD([sQuery(id+"F0.wireOp",EDGE,"E20.top"),sQuery(id+"F2.wireOp",EDGE,"E142.bottom"),sQuery(id+"F2.wireOp",EDGE,"E142.left"),sQuery(id+"F2.wireOp",EDGE,"E142.right"),sQuery(id+"F4.wireOp",EDGE,"E146.bottom"),sQuery(id+"F4.wireOp",EDGE,"E146.left"),sQuery(id+"F4.wireOp",EDGE,"E146.right")])]});
            var Q5;
            Q5=makeQuery(id+"F8.opLoft","SWEPT_FACE",FACE,{"disambiguationData":[OSD([sQuery(id+"F0.wireOp",EDGE,"E20.bottom"),sQuery(id+"F2.wireOp",EDGE,"E143.bottom"),sQuery(id+"F2.wireOp",EDGE,"E143.left"),sQuery(id+"F2.wireOp",EDGE,"E143.right"),sQuery(id+"F4.wireOp",EDGE,"E147.bottom"),sQuery(id+"F4.wireOp",EDGE,"E147.left"),sQuery(id+"F4.wireOp",EDGE,"E147.right")])]});
            var Q6;
            Q6=makeQuery(id+"F8.opLoft","SWEPT_FACE",FACE,{"disambiguationData":[OSD([sQuery(id+"F0.wireOp",EDGE,"E20.right"),sQuery(id+"F2.wireOp",EDGE,"E143.bottom"),sQuery(id+"F2.wireOp",EDGE,"E143.top"),sQuery(id+"F2.wireOp",EDGE,"E143.left"),sQuery(id+"F4.wireOp",EDGE,"E147.bottom"),sQuery(id+"F4.wireOp",EDGE,"E147.top"),sQuery(id+"F4.wireOp",EDGE,"E147.left")])]});
            var Q7;
            Q7=makeQuery(id+"F7.opLoft","SWEPT_FACE",FACE,{"disambiguationData":[OSD([sQuery(id+"F0.wireOp",EDGE,"E20.bottom"),sQuery(id+"F2.wireOp",EDGE,"E144.bottom"),sQuery(id+"F2.wireOp",EDGE,"E144.left"),sQuery(id+"F2.wireOp",EDGE,"E144.right"),sQuery(id+"F4.wireOp",EDGE,"E148.bottom"),sQuery(id+"F4.wireOp",EDGE,"E148.left"),sQuery(id+"F4.wireOp",EDGE,"E148.right")])]});
            var Q8;
            Q8=makeQuery(id+"F7.opLoft","SWEPT_FACE",FACE,{"disambiguationData":[OSD([sQuery(id+"F0.wireOp",EDGE,"E20.left"),sQuery(id+"F2.wireOp",EDGE,"E144.bottom"),sQuery(id+"F2.wireOp",EDGE,"E144.top"),sQuery(id+"F2.wireOp",EDGE,"E144.left"),sQuery(id+"F4.wireOp",EDGE,"E148.bottom"),sQuery(id+"F4.wireOp",EDGE,"E148.top"),sQuery(id+"F4.wireOp",EDGE,"E148.left")])]});
            shell(context, id + "F9", {"entities" : qUnion([Q0, Q1, Q2, Q3, Q4, Q5, Q6, Q7, Q8]), "thickness" : 1 * mm});
        }
        {
            var Q0;
            Q0=qCreatedBy(id+"F3.planeOp",FACE);
            var sketch = newSketch(context, id + "F10", { "sketchPlane" : qUnion([Q0])});
            skLineSegment(sketch, "E149.bottom", {"start": v(-125, 110) * mm, "end": v(125, 110) * mm});
            skLineSegment(sketch, "E149.top", {"start": v(-125, -110) * mm, "end": v(125, -110) * mm});
            skLineSegment(sketch, "E149.left", {"start": v(-125, 110) * mm, "end": v(-125, -110) * mm});
            skLineSegment(sketch, "E149.right", {"start": v(125, 110) * mm, "end": v(125, -110) * mm});
            skSolve(sketch);
        }
        {
            var Q0;
            Q0=makeQuery(id+"F10.imprint","IMPRINT",FACE,{"disambiguationData":[TD([[makeQuery(id+"F10.imprint","IMPRINT",EDGE,{"derivedFrom":sQuery(id+"F10.wireOp",EDGE,"E149.bottom")}),-1.0]])]});
            extrude(context, id + "F11", {"entities" : qUnion([Q0]), "depth" : 1 * mm});
        }
        {
            var Q0;
            Q0=makeQuery(id+"F11.opExtrude","CAP_FACE",FACE,{"disambiguationData":[OSD([sQuery(id+"F10.wireOp",EDGE,"E149.bottom"),sQuery(id+"F10.wireOp",EDGE,"E149.top"),sQuery(id+"F10.wireOp",EDGE,"E149.left"),sQuery(id+"F10.wireOp",EDGE,"E149.right")])],"isStart":false});
            var sketch = newSketch(context, id + "F12", { "sketchPlane" : qUnion([Q0])});
            skLineSegment(sketch, "E150.bottom", {"start": v(-119.08, 104) * mm, "end": v(119, 104) * mm, "construction": true});
            skLineSegment(sketch, "E150.top", {"start": v(-119.08, -104) * mm, "end": v(119, -104) * mm, "construction": true});
            skLineSegment(sketch, "E150.left", {"start": v(-119.08, 104) * mm, "end": v(-119.08, -104) * mm, "construction": true});
            skLineSegment(sketch, "E150.right", {"start": v(119, 104) * mm, "end": v(119, -104) * mm, "construction": true});
            skCircle(sketch, "E151", {"center": v(-119.08, 104) * mm, "radius": 2.75 * mm});
            skCircle(sketch, "E152", {"center": v(-119.08, -104) * mm, "radius": 2.75 * mm});
            skCircle(sketch, "E153", {"center": v(119, -104) * mm, "radius": 2.75 * mm});
            skCircle(sketch, "E154", {"center": v(119, 104) * mm, "radius": 2.75 * mm});
            skSolve(sketch);
        }
        {
            var Q0;
            Q0 = qSketchRegion(id + "F12", true);
            extrude(context, id + "F13", {"entities" : qUnion([Q0]), "operationType" : NewBodyOperationType.REMOVE, "oppositeDirection" : true, "depth" : 25 * mm});
        }
        {
            var Q0;
            Q0=makeQuery(id+"F1.opExtrude","CAP_FACE",FACE,{"disambiguationData":[OSD([sQuery(id+"F0.wireOp",EDGE,"E20.bottom"),sQuery(id+"F0.wireOp",EDGE,"E20.top"),sQuery(id+"F0.wireOp",EDGE,"E20.left"),sQuery(id+"F0.wireOp",EDGE,"E20.right"),sQuery(id+"F0.wireOp",EDGE,"E24.bottom"),sQuery(id+"F0.wireOp",EDGE,"E24.top"),sQuery(id+"F0.wireOp",EDGE,"E24.left"),sQuery(id+"F0.wireOp",EDGE,"E24.right"),sQuery(id+"F0.wireOp",EDGE,"E25.filletArc"),sQuery(id+"F0.wireOp",EDGE,"E26.filletArc"),sQuery(id+"F0.wireOp",EDGE,"E27.filletArc"),sQuery(id+"F0.wireOp",EDGE,"E28.filletArc"),sQuery(id+"F0.wireOp",EDGE,"E31.0.startCap"),sQuery(id+"F0.wireOp",EDGE,"E31.0.endCap"),sQuery(id+"F0.wireOp",EDGE,"E31.0.left"),sQuery(id+"F0.wireOp",EDGE,"E31.0.right"),sQuery(id+"F0.wireOp",EDGE,"E32"),sQuery(id+"F0.wireOp",EDGE,"E33"),sQuery(id+"F0.wireOp",EDGE,"E34"),sQuery(id+"F0.wireOp",EDGE,"E35"),sQuery(id+"F0.wireOp",EDGE,"E42"),sQuery(id+"F0.wireOp",EDGE,"E43"),sQuery(id+"F0.wireOp",EDGE,"E44"),sQuery(id+"F0.wireOp",EDGE,"E47.top"),sQuery(id+"F0.wireOp",EDGE,"E47.right"),sQuery(id+"F0.wireOp",EDGE,"E39.filletArc"),sQuery(id+"F0.wireOp",EDGE,"E38.filletArc"),sQuery(id+"F0.wireOp",EDGE,"E47.left"),sQuery(id+"F0.wireOp",EDGE,"E36.filletArc"),sQuery(id+"F0.wireOp",EDGE,"E37.filletArc"),sQuery(id+"F0.wireOp",EDGE,"E47.bottom"),sQuery(id+"F0.wireOp",EDGE,"E48"),sQuery(id+"F0.wireOp",EDGE,"E49.0.endCap"),sQuery(id+"F0.wireOp",EDGE,"E49.0.startCap"),sQuery(id+"F0.wireOp",EDGE,"E49.0.right"),sQuery(id+"F0.wireOp",EDGE,"E49.0.left"),sQuery(id+"F0.wireOp",EDGE,"E57"),sQuery(id+"F0.wireOp",EDGE,"E58"),sQuery(id+"F0.wireOp",EDGE,"E59"),sQuery(id+"F0.wireOp",EDGE,"E62.top"),sQuery(id+"F0.wireOp",EDGE,"E62.right"),sQuery(id+"F0.wireOp",EDGE,"E54.filletArc"),sQuery(id+"F0.wireOp",EDGE,"E53.filletArc"),sQuery(id+"F0.wireOp",EDGE,"E62.left"),sQuery(id+"F0.wireOp",EDGE,"E51.filletArc"),sQuery(id+"F0.wireOp",EDGE,"E52.filletArc"),sQuery(id+"F0.wireOp",EDGE,"E62.bottom"),sQuery(id+"F0.wireOp",EDGE,"E63"),sQuery(id+"F0.wireOp",EDGE,"E64.0.endCap"),sQuery(id+"F0.wireOp",EDGE,"E64.0.startCap"),sQuery(id+"F0.wireOp",EDGE,"E64.0.right"),sQuery(id+"F0.wireOp",EDGE,"E64.0.left"),sQuery(id+"F0.wireOp",EDGE,"E72"),sQuery(id+"F0.wireOp",EDGE,"E73"),sQuery(id+"F0.wireOp",EDGE,"E74"),sQuery(id+"F0.wireOp",EDGE,"E77.top"),sQuery(id+"F0.wireOp",EDGE,"E77.right"),sQuery(id+"F0.wireOp",EDGE,"E69.filletArc"),sQuery(id+"F0.wireOp",EDGE,"E68.filletArc"),sQuery(id+"F0.wireOp",EDGE,"E77.left"),sQuery(id+"F0.wireOp",EDGE,"E66.filletArc"),sQuery(id+"F0.wireOp",EDGE,"E67.filletArc"),sQuery(id+"F0.wireOp",EDGE,"E77.bottom"),sQuery(id+"F0.wireOp",EDGE,"E78"),sQuery(id+"F0.wireOp",EDGE,"E79.0.endCap"),sQuery(id+"F0.wireOp",EDGE,"E79.0.startCap"),sQuery(id+"F0.wireOp",EDGE,"E79.0.right"),sQuery(id+"F0.wireOp",EDGE,"E79.0.left"),sQuery(id+"F0.wireOp",EDGE,"E87"),sQuery(id+"F0.wireOp",EDGE,"E88"),sQuery(id+"F0.wireOp",EDGE,"E89"),sQuery(id+"F0.wireOp",EDGE,"E92.top"),sQuery(id+"F0.wireOp",EDGE,"E92.right"),sQuery(id+"F0.wireOp",EDGE,"E84.filletArc"),sQuery(id+"F0.wireOp",EDGE,"E83.filletArc"),sQuery(id+"F0.wireOp",EDGE,"E92.left"),sQuery(id+"F0.wireOp",EDGE,"E81.filletArc"),sQuery(id+"F0.wireOp",EDGE,"E82.filletArc"),sQuery(id+"F0.wireOp",EDGE,"E92.bottom"),sQuery(id+"F0.wireOp",EDGE,"E93"),sQuery(id+"F0.wireOp",EDGE,"E94.0.endCap"),sQuery(id+"F0.wireOp",EDGE,"E94.0.startCap"),sQuery(id+"F0.wireOp",EDGE,"E94.0.right"),sQuery(id+"F0.wireOp",EDGE,"E94.0.left"),sQuery(id+"F0.wireOp",EDGE,"E102"),sQuery(id+"F0.wireOp",EDGE,"E103"),sQuery(id+"F0.wireOp",EDGE,"E104"),sQuery(id+"F0.wireOp",EDGE,"E107.top"),sQuery(id+"F0.wireOp",EDGE,"E107.right"),sQuery(id+"F0.wireOp",EDGE,"E99.filletArc"),sQuery(id+"F0.wireOp",EDGE,"E98.filletArc"),sQuery(id+"F0.wireOp",EDGE,"E107.left"),sQuery(id+"F0.wireOp",EDGE,"E96.filletArc"),sQuery(id+"F0.wireOp",EDGE,"E97.filletArc"),sQuery(id+"F0.wireOp",EDGE,"E107.bottom"),sQuery(id+"F0.wireOp",EDGE,"E108"),sQuery(id+"F0.wireOp",EDGE,"E109.0.endCap"),sQuery(id+"F0.wireOp",EDGE,"E109.0.startCap"),sQuery(id+"F0.wireOp",EDGE,"E109.0.right"),sQuery(id+"F0.wireOp",EDGE,"E109.0.left"),sQuery(id+"F0.wireOp",EDGE,"E117"),sQuery(id+"F0.wireOp",EDGE,"E118"),sQuery(id+"F0.wireOp",EDGE,"E119"),sQuery(id+"F0.wireOp",EDGE,"E122.top"),sQuery(id+"F0.wireOp",EDGE,"E122.right"),sQuery(id+"F0.wireOp",EDGE,"E114.filletArc"),sQuery(id+"F0.wireOp",EDGE,"E113.filletArc"),sQuery(id+"F0.wireOp",EDGE,"E122.left"),sQuery(id+"F0.wireOp",EDGE,"E111.filletArc"),sQuery(id+"F0.wireOp",EDGE,"E112.filletArc"),sQuery(id+"F0.wireOp",EDGE,"E122.bottom"),sQuery(id+"F0.wireOp",EDGE,"E123"),sQuery(id+"F0.wireOp",EDGE,"E124.0.endCap"),sQuery(id+"F0.wireOp",EDGE,"E124.0.startCap"),sQuery(id+"F0.wireOp",EDGE,"E124.0.right"),sQuery(id+"F0.wireOp",EDGE,"E124.0.left"),sQuery(id+"F0.wireOp",EDGE,"E132"),sQuery(id+"F0.wireOp",EDGE,"E133"),sQuery(id+"F0.wireOp",EDGE,"E134"),sQuery(id+"F0.wireOp",EDGE,"E137.top"),sQuery(id+"F0.wireOp",EDGE,"E137.right"),sQuery(id+"F0.wireOp",EDGE,"E129.filletArc"),sQuery(id+"F0.wireOp",EDGE,"E128.filletArc"),sQuery(id+"F0.wireOp",EDGE,"E137.left"),sQuery(id+"F0.wireOp",EDGE,"E126.filletArc"),sQuery(id+"F0.wireOp",EDGE,"E127.filletArc"),sQuery(id+"F0.wireOp",EDGE,"E137.bottom"),sQuery(id+"F0.wireOp",EDGE,"E138"),sQuery(id+"F0.wireOp",EDGE,"E139.0.endCap"),sQuery(id+"F0.wireOp",EDGE,"E139.0.startCap"),sQuery(id+"F0.wireOp",EDGE,"E139.0.right"),sQuery(id+"F0.wireOp",EDGE,"E139.0.left")])],"isStart":false});
            var sketch = newSketch(context, id + "F14", { "sketchPlane" : qUnion([Q0])});
            skLineSegment(sketch, "E155.bottom", {"start": v(130, 115) * mm, "end": v(-130, 115) * mm, "construction": true});
            skLineSegment(sketch, "E155.top", {"start": v(130, -115) * mm, "end": v(-130, -115) * mm, "construction": true});
            skLineSegment(sketch, "E155.left", {"start": v(130, 115) * mm, "end": v(130, -115) * mm, "construction": true});
            skLineSegment(sketch, "E155.right", {"start": v(-130, 115) * mm, "end": v(-130, -115) * mm, "construction": true});
            skPoint(sketch, "E156", {"position": v(130, 115) * mm});
            skPoint(sketch, "E157", {"position": v(130, -115) * mm});
            skPoint(sketch, "E158", {"position": v(-130, -115) * mm});
            skPoint(sketch, "E159", {"position": v(-130, 115) * mm});
            skSolve(sketch);
        }
        {
            var Q0;
            Q0=sQuery(id+"F14.wireOp",VERTEX,"E156");
            var Q1;
            Q1=sQuery(id+"F14.wireOp",VERTEX,"E157");
            var Q2;
            Q2=sQuery(id+"F14.wireOp",VERTEX,"E158");
            var Q3;
            Q3=sQuery(id+"F14.wireOp",VERTEX,"E159");
            var Q4;
            Q4=makeQuery(id+"F1.opExtrude","SWEPT_BODY",BODY,{"disambiguationData":[OSD([sQuery(id+"F0.wireOp",EDGE,"E20.bottom"),sQuery(id+"F0.wireOp",EDGE,"E20.top"),sQuery(id+"F0.wireOp",EDGE,"E20.left"),sQuery(id+"F0.wireOp",EDGE,"E20.right"),sQuery(id+"F0.wireOp",EDGE,"E24.bottom"),sQuery(id+"F0.wireOp",EDGE,"E24.top"),sQuery(id+"F0.wireOp",EDGE,"E24.left"),sQuery(id+"F0.wireOp",EDGE,"E24.right"),sQuery(id+"F0.wireOp",EDGE,"E25.filletArc"),sQuery(id+"F0.wireOp",EDGE,"E26.filletArc"),sQuery(id+"F0.wireOp",EDGE,"E27.filletArc"),sQuery(id+"F0.wireOp",EDGE,"E28.filletArc"),sQuery(id+"F0.wireOp",EDGE,"E31.0.startCap"),sQuery(id+"F0.wireOp",EDGE,"E31.0.endCap"),sQuery(id+"F0.wireOp",EDGE,"E31.0.left"),sQuery(id+"F0.wireOp",EDGE,"E31.0.right"),sQuery(id+"F0.wireOp",EDGE,"E32"),sQuery(id+"F0.wireOp",EDGE,"E33"),sQuery(id+"F0.wireOp",EDGE,"E34"),sQuery(id+"F0.wireOp",EDGE,"E35"),sQuery(id+"F0.wireOp",EDGE,"E42"),sQuery(id+"F0.wireOp",EDGE,"E43"),sQuery(id+"F0.wireOp",EDGE,"E44"),sQuery(id+"F0.wireOp",EDGE,"E47.top"),sQuery(id+"F0.wireOp",EDGE,"E47.right"),sQuery(id+"F0.wireOp",EDGE,"E39.filletArc"),sQuery(id+"F0.wireOp",EDGE,"E38.filletArc"),sQuery(id+"F0.wireOp",EDGE,"E47.left"),sQuery(id+"F0.wireOp",EDGE,"E36.filletArc"),sQuery(id+"F0.wireOp",EDGE,"E37.filletArc"),sQuery(id+"F0.wireOp",EDGE,"E47.bottom"),sQuery(id+"F0.wireOp",EDGE,"E48"),sQuery(id+"F0.wireOp",EDGE,"E49.0.endCap"),sQuery(id+"F0.wireOp",EDGE,"E49.0.startCap"),sQuery(id+"F0.wireOp",EDGE,"E49.0.right"),sQuery(id+"F0.wireOp",EDGE,"E49.0.left"),sQuery(id+"F0.wireOp",EDGE,"E57"),sQuery(id+"F0.wireOp",EDGE,"E58"),sQuery(id+"F0.wireOp",EDGE,"E59"),sQuery(id+"F0.wireOp",EDGE,"E62.top"),sQuery(id+"F0.wireOp",EDGE,"E62.right"),sQuery(id+"F0.wireOp",EDGE,"E54.filletArc"),sQuery(id+"F0.wireOp",EDGE,"E53.filletArc"),sQuery(id+"F0.wireOp",EDGE,"E62.left"),sQuery(id+"F0.wireOp",EDGE,"E51.filletArc"),sQuery(id+"F0.wireOp",EDGE,"E52.filletArc"),sQuery(id+"F0.wireOp",EDGE,"E62.bottom"),sQuery(id+"F0.wireOp",EDGE,"E63"),sQuery(id+"F0.wireOp",EDGE,"E64.0.endCap"),sQuery(id+"F0.wireOp",EDGE,"E64.0.startCap"),sQuery(id+"F0.wireOp",EDGE,"E64.0.right"),sQuery(id+"F0.wireOp",EDGE,"E64.0.left"),sQuery(id+"F0.wireOp",EDGE,"E72"),sQuery(id+"F0.wireOp",EDGE,"E73"),sQuery(id+"F0.wireOp",EDGE,"E74"),sQuery(id+"F0.wireOp",EDGE,"E77.top"),sQuery(id+"F0.wireOp",EDGE,"E77.right"),sQuery(id+"F0.wireOp",EDGE,"E69.filletArc"),sQuery(id+"F0.wireOp",EDGE,"E68.filletArc"),sQuery(id+"F0.wireOp",EDGE,"E77.left"),sQuery(id+"F0.wireOp",EDGE,"E66.filletArc"),sQuery(id+"F0.wireOp",EDGE,"E67.filletArc"),sQuery(id+"F0.wireOp",EDGE,"E77.bottom"),sQuery(id+"F0.wireOp",EDGE,"E78"),sQuery(id+"F0.wireOp",EDGE,"E79.0.endCap"),sQuery(id+"F0.wireOp",EDGE,"E79.0.startCap"),sQuery(id+"F0.wireOp",EDGE,"E79.0.right"),sQuery(id+"F0.wireOp",EDGE,"E79.0.left"),sQuery(id+"F0.wireOp",EDGE,"E87"),sQuery(id+"F0.wireOp",EDGE,"E88"),sQuery(id+"F0.wireOp",EDGE,"E89"),sQuery(id+"F0.wireOp",EDGE,"E92.top"),sQuery(id+"F0.wireOp",EDGE,"E92.right"),sQuery(id+"F0.wireOp",EDGE,"E84.filletArc"),sQuery(id+"F0.wireOp",EDGE,"E83.filletArc"),sQuery(id+"F0.wireOp",EDGE,"E92.left"),sQuery(id+"F0.wireOp",EDGE,"E81.filletArc"),sQuery(id+"F0.wireOp",EDGE,"E82.filletArc"),sQuery(id+"F0.wireOp",EDGE,"E92.bottom"),sQuery(id+"F0.wireOp",EDGE,"E93"),sQuery(id+"F0.wireOp",EDGE,"E94.0.endCap"),sQuery(id+"F0.wireOp",EDGE,"E94.0.startCap"),sQuery(id+"F0.wireOp",EDGE,"E94.0.right"),sQuery(id+"F0.wireOp",EDGE,"E94.0.left"),sQuery(id+"F0.wireOp",EDGE,"E102"),sQuery(id+"F0.wireOp",EDGE,"E103"),sQuery(id+"F0.wireOp",EDGE,"E104"),sQuery(id+"F0.wireOp",EDGE,"E107.top"),sQuery(id+"F0.wireOp",EDGE,"E107.right"),sQuery(id+"F0.wireOp",EDGE,"E99.filletArc"),sQuery(id+"F0.wireOp",EDGE,"E98.filletArc"),sQuery(id+"F0.wireOp",EDGE,"E107.left"),sQuery(id+"F0.wireOp",EDGE,"E96.filletArc"),sQuery(id+"F0.wireOp",EDGE,"E97.filletArc"),sQuery(id+"F0.wireOp",EDGE,"E107.bottom"),sQuery(id+"F0.wireOp",EDGE,"E108"),sQuery(id+"F0.wireOp",EDGE,"E109.0.endCap"),sQuery(id+"F0.wireOp",EDGE,"E109.0.startCap"),sQuery(id+"F0.wireOp",EDGE,"E109.0.right"),sQuery(id+"F0.wireOp",EDGE,"E109.0.left"),sQuery(id+"F0.wireOp",EDGE,"E117"),sQuery(id+"F0.wireOp",EDGE,"E118"),sQuery(id+"F0.wireOp",EDGE,"E119"),sQuery(id+"F0.wireOp",EDGE,"E122.top"),sQuery(id+"F0.wireOp",EDGE,"E122.right"),sQuery(id+"F0.wireOp",EDGE,"E114.filletArc"),sQuery(id+"F0.wireOp",EDGE,"E113.filletArc"),sQuery(id+"F0.wireOp",EDGE,"E122.left"),sQuery(id+"F0.wireOp",EDGE,"E111.filletArc"),sQuery(id+"F0.wireOp",EDGE,"E112.filletArc"),sQuery(id+"F0.wireOp",EDGE,"E122.bottom"),sQuery(id+"F0.wireOp",EDGE,"E123"),sQuery(id+"F0.wireOp",EDGE,"E124.0.endCap"),sQuery(id+"F0.wireOp",EDGE,"E124.0.startCap"),sQuery(id+"F0.wireOp",EDGE,"E124.0.right"),sQuery(id+"F0.wireOp",EDGE,"E124.0.left"),sQuery(id+"F0.wireOp",EDGE,"E132"),sQuery(id+"F0.wireOp",EDGE,"E133"),sQuery(id+"F0.wireOp",EDGE,"E134"),sQuery(id+"F0.wireOp",EDGE,"E137.top"),sQuery(id+"F0.wireOp",EDGE,"E137.right"),sQuery(id+"F0.wireOp",EDGE,"E129.filletArc"),sQuery(id+"F0.wireOp",EDGE,"E128.filletArc"),sQuery(id+"F0.wireOp",EDGE,"E137.left"),sQuery(id+"F0.wireOp",EDGE,"E126.filletArc"),sQuery(id+"F0.wireOp",EDGE,"E127.filletArc"),sQuery(id+"F0.wireOp",EDGE,"E137.bottom"),sQuery(id+"F0.wireOp",EDGE,"E138"),sQuery(id+"F0.wireOp",EDGE,"E139.0.endCap"),sQuery(id+"F0.wireOp",EDGE,"E139.0.startCap"),sQuery(id+"F0.wireOp",EDGE,"E139.0.right"),sQuery(id+"F0.wireOp",EDGE,"E139.0.left")])]});
            var Q5;
            Q5=makeQuery(id+"F8.opLoft","SWEPT_BODY",BODY,{"disambiguationData":[OSD([makeQuery(id+"F2.imprint","IMPRINT",FACE,{"disambiguationData":[TD([[makeQuery(id+"F2.imprint","IMPRINT",EDGE,{"derivedFrom":sQuery(id+"F2.wireOp",EDGE,"E143.bottom")}),1.0]])]}),makeQuery(id+"F4.imprint","IMPRINT",FACE,{"disambiguationData":[TD([[makeQuery(id+"F4.imprint","IMPRINT",EDGE,{"derivedFrom":sQuery(id+"F4.wireOp",EDGE,"E147.bottom")}),-1.0]])]})])]});
            var Q6;
            Q6=makeQuery(id+"F7.opLoft","SWEPT_BODY",BODY,{"disambiguationData":[OSD([makeQuery(id+"F2.imprint","IMPRINT",FACE,{"disambiguationData":[TD([[makeQuery(id+"F2.imprint","IMPRINT",EDGE,{"derivedFrom":sQuery(id+"F2.wireOp",EDGE,"E144.bottom")}),1.0]])]}),makeQuery(id+"F4.imprint","IMPRINT",FACE,{"disambiguationData":[TD([[makeQuery(id+"F4.imprint","IMPRINT",EDGE,{"derivedFrom":sQuery(id+"F4.wireOp",EDGE,"E148.bottom")}),1.0]])]})])]});
            var Q7;
            Q7=makeQuery(id+"F5.opLoft","SWEPT_BODY",BODY,{"disambiguationData":[OSD([makeQuery(id+"F2.imprint","IMPRINT",FACE,{"disambiguationData":[TD([[makeQuery(id+"F2.imprint","IMPRINT",EDGE,{"derivedFrom":sQuery(id+"F2.wireOp",EDGE,"E141.bottom")}),-1.0]])]}),makeQuery(id+"F4.imprint","IMPRINT",FACE,{"disambiguationData":[TD([[makeQuery(id+"F4.imprint","IMPRINT",EDGE,{"derivedFrom":sQuery(id+"F4.wireOp",EDGE,"E145.bottom")}),-1.0]])]})])]});
            var Q8;
            Q8=makeQuery(id+"F6.opLoft","SWEPT_BODY",BODY,{"disambiguationData":[OSD([makeQuery(id+"F2.imprint","IMPRINT",FACE,{"disambiguationData":[TD([[makeQuery(id+"F2.imprint","IMPRINT",EDGE,{"derivedFrom":sQuery(id+"F2.wireOp",EDGE,"E142.bottom")}),-1.0]])]}),makeQuery(id+"F4.imprint","IMPRINT",FACE,{"disambiguationData":[TD([[makeQuery(id+"F4.imprint","IMPRINT",EDGE,{"derivedFrom":sQuery(id+"F4.wireOp",EDGE,"E146.bottom")}),1.0]])]})])]});
            hole(context, id + "F15", {"style" : HoleStyle.C_BORE, "holeDiameter" : 5.5 * mm, "cBoreDiameter" : 9 * mm, "cBoreDepth" : 5.5 * mm, "endStyle" : HoleEndStyle.BLIND, "holeDepth" : 20 * mm, "locations" : qUnion([Q0, Q1, Q2, Q3]), "scope" : qUnion([Q4, Q5, Q6, Q7, Q8])});
        }
        {
            var Q0;
            Q0=makeQuery(id+"F5.opLoft","SWEPT_EDGE",EDGE,{"disambiguationData":[OSD([sQuery(id+"F2.wireOp",EDGE,"E141.top"),sQuery(id+"F2.wireOp",EDGE,"E141.right"),sQuery(id+"F4.wireOp",EDGE,"E145.top"),sQuery(id+"F4.wireOp",EDGE,"E145.right")])]});
            var Q1;
            Q1=makeQuery(id+"F6.opLoft","SWEPT_EDGE",EDGE,{"disambiguationData":[OSD([sQuery(id+"F2.wireOp",EDGE,"E142.top"),sQuery(id+"F2.wireOp",EDGE,"E142.right"),sQuery(id+"F4.wireOp",EDGE,"E146.top"),sQuery(id+"F4.wireOp",EDGE,"E146.right")])]});
            var Q2;
            Q2=makeQuery(id+"F7.opLoft","SWEPT_EDGE",EDGE,{"disambiguationData":[OSD([sQuery(id+"F2.wireOp",EDGE,"E144.top"),sQuery(id+"F2.wireOp",EDGE,"E144.right"),sQuery(id+"F4.wireOp",EDGE,"E148.top"),sQuery(id+"F4.wireOp",EDGE,"E148.right")])]});
            var Q3;
            Q3=makeQuery(id+"F8.opLoft","SWEPT_EDGE",EDGE,{"disambiguationData":[OSD([sQuery(id+"F2.wireOp",EDGE,"E143.top"),sQuery(id+"F2.wireOp",EDGE,"E143.right"),sQuery(id+"F4.wireOp",EDGE,"E147.top"),sQuery(id+"F4.wireOp",EDGE,"E147.right")])]});
            fillet(context, id + "F16", {"entities" : qUnion([Q0, Q1, Q2, Q3]), "radius" : 2 * mm, "tangentPropagation" : true, "allowEdgeOverflow" : false});
        }
        {
            var Q0;
            Q0=makeQuery(id+"F9.opShell","OFFSET_EDGE",EDGE,{"disambiguationData":[OSD([sQuery(id+"F2.wireOp",EDGE,"E142.top"),sQuery(id+"F2.wireOp",EDGE,"E142.right"),sQuery(id+"F4.wireOp",EDGE,"E146.top"),sQuery(id+"F4.wireOp",EDGE,"E146.right")])]});
            var Q1;
            Q1=makeQuery(id+"F9.opShell","OFFSET_EDGE",EDGE,{"disambiguationData":[OSD([sQuery(id+"F2.wireOp",EDGE,"E143.top"),sQuery(id+"F2.wireOp",EDGE,"E143.right"),sQuery(id+"F4.wireOp",EDGE,"E147.top"),sQuery(id+"F4.wireOp",EDGE,"E147.right")])]});
            var Q2;
            Q2=makeQuery(id+"F9.opShell","OFFSET_EDGE",EDGE,{"disambiguationData":[OSD([sQuery(id+"F2.wireOp",EDGE,"E144.top"),sQuery(id+"F2.wireOp",EDGE,"E144.right"),sQuery(id+"F4.wireOp",EDGE,"E148.top"),sQuery(id+"F4.wireOp",EDGE,"E148.right")])]});
            var Q3;
            Q3=makeQuery(id+"F9.opShell","OFFSET_EDGE",EDGE,{"disambiguationData":[OSD([sQuery(id+"F2.wireOp",EDGE,"E141.top"),sQuery(id+"F2.wireOp",EDGE,"E141.right"),sQuery(id+"F4.wireOp",EDGE,"E145.top"),sQuery(id+"F4.wireOp",EDGE,"E145.right")])]});
            fillet(context, id + "F17", {"entities" : qUnion([Q0, Q1, Q2, Q3]), "radius" : 1 * mm, "tangentPropagation" : true, "allowEdgeOverflow" : false});
        }
        {
            var Q0;
            Q0=makeQuery(id+"F1.opExtrude","CAP_FACE",FACE,{"disambiguationData":[OSD([sQuery(id+"F0.wireOp",EDGE,"E20.bottom"),sQuery(id+"F0.wireOp",EDGE,"E20.top"),sQuery(id+"F0.wireOp",EDGE,"E20.left"),sQuery(id+"F0.wireOp",EDGE,"E20.right"),sQuery(id+"F0.wireOp",EDGE,"E24.bottom"),sQuery(id+"F0.wireOp",EDGE,"E24.top"),sQuery(id+"F0.wireOp",EDGE,"E24.left"),sQuery(id+"F0.wireOp",EDGE,"E24.right"),sQuery(id+"F0.wireOp",EDGE,"E25.filletArc"),sQuery(id+"F0.wireOp",EDGE,"E26.filletArc"),sQuery(id+"F0.wireOp",EDGE,"E27.filletArc"),sQuery(id+"F0.wireOp",EDGE,"E28.filletArc"),sQuery(id+"F0.wireOp",EDGE,"E31.0.startCap"),sQuery(id+"F0.wireOp",EDGE,"E31.0.endCap"),sQuery(id+"F0.wireOp",EDGE,"E31.0.left"),sQuery(id+"F0.wireOp",EDGE,"E31.0.right"),sQuery(id+"F0.wireOp",EDGE,"E32"),sQuery(id+"F0.wireOp",EDGE,"E33"),sQuery(id+"F0.wireOp",EDGE,"E34"),sQuery(id+"F0.wireOp",EDGE,"E35"),sQuery(id+"F0.wireOp",EDGE,"E42"),sQuery(id+"F0.wireOp",EDGE,"E43"),sQuery(id+"F0.wireOp",EDGE,"E44"),sQuery(id+"F0.wireOp",EDGE,"E47.top"),sQuery(id+"F0.wireOp",EDGE,"E47.right"),sQuery(id+"F0.wireOp",EDGE,"E39.filletArc"),sQuery(id+"F0.wireOp",EDGE,"E38.filletArc"),sQuery(id+"F0.wireOp",EDGE,"E47.left"),sQuery(id+"F0.wireOp",EDGE,"E36.filletArc"),sQuery(id+"F0.wireOp",EDGE,"E37.filletArc"),sQuery(id+"F0.wireOp",EDGE,"E47.bottom"),sQuery(id+"F0.wireOp",EDGE,"E48"),sQuery(id+"F0.wireOp",EDGE,"E49.0.endCap"),sQuery(id+"F0.wireOp",EDGE,"E49.0.startCap"),sQuery(id+"F0.wireOp",EDGE,"E49.0.right"),sQuery(id+"F0.wireOp",EDGE,"E49.0.left"),sQuery(id+"F0.wireOp",EDGE,"E57"),sQuery(id+"F0.wireOp",EDGE,"E58"),sQuery(id+"F0.wireOp",EDGE,"E59"),sQuery(id+"F0.wireOp",EDGE,"E62.top"),sQuery(id+"F0.wireOp",EDGE,"E62.right"),sQuery(id+"F0.wireOp",EDGE,"E54.filletArc"),sQuery(id+"F0.wireOp",EDGE,"E53.filletArc"),sQuery(id+"F0.wireOp",EDGE,"E62.left"),sQuery(id+"F0.wireOp",EDGE,"E51.filletArc"),sQuery(id+"F0.wireOp",EDGE,"E52.filletArc"),sQuery(id+"F0.wireOp",EDGE,"E62.bottom"),sQuery(id+"F0.wireOp",EDGE,"E63"),sQuery(id+"F0.wireOp",EDGE,"E64.0.endCap"),sQuery(id+"F0.wireOp",EDGE,"E64.0.startCap"),sQuery(id+"F0.wireOp",EDGE,"E64.0.right"),sQuery(id+"F0.wireOp",EDGE,"E64.0.left"),sQuery(id+"F0.wireOp",EDGE,"E72"),sQuery(id+"F0.wireOp",EDGE,"E73"),sQuery(id+"F0.wireOp",EDGE,"E74"),sQuery(id+"F0.wireOp",EDGE,"E77.top"),sQuery(id+"F0.wireOp",EDGE,"E77.right"),sQuery(id+"F0.wireOp",EDGE,"E69.filletArc"),sQuery(id+"F0.wireOp",EDGE,"E68.filletArc"),sQuery(id+"F0.wireOp",EDGE,"E77.left"),sQuery(id+"F0.wireOp",EDGE,"E66.filletArc"),sQuery(id+"F0.wireOp",EDGE,"E67.filletArc"),sQuery(id+"F0.wireOp",EDGE,"E77.bottom"),sQuery(id+"F0.wireOp",EDGE,"E78"),sQuery(id+"F0.wireOp",EDGE,"E79.0.endCap"),sQuery(id+"F0.wireOp",EDGE,"E79.0.startCap"),sQuery(id+"F0.wireOp",EDGE,"E79.0.right"),sQuery(id+"F0.wireOp",EDGE,"E79.0.left"),sQuery(id+"F0.wireOp",EDGE,"E87"),sQuery(id+"F0.wireOp",EDGE,"E88"),sQuery(id+"F0.wireOp",EDGE,"E89"),sQuery(id+"F0.wireOp",EDGE,"E92.top"),sQuery(id+"F0.wireOp",EDGE,"E92.right"),sQuery(id+"F0.wireOp",EDGE,"E84.filletArc"),sQuery(id+"F0.wireOp",EDGE,"E83.filletArc"),sQuery(id+"F0.wireOp",EDGE,"E92.left"),sQuery(id+"F0.wireOp",EDGE,"E81.filletArc"),sQuery(id+"F0.wireOp",EDGE,"E82.filletArc"),sQuery(id+"F0.wireOp",EDGE,"E92.bottom"),sQuery(id+"F0.wireOp",EDGE,"E93"),sQuery(id+"F0.wireOp",EDGE,"E94.0.endCap"),sQuery(id+"F0.wireOp",EDGE,"E94.0.startCap"),sQuery(id+"F0.wireOp",EDGE,"E94.0.right"),sQuery(id+"F0.wireOp",EDGE,"E94.0.left"),sQuery(id+"F0.wireOp",EDGE,"E102"),sQuery(id+"F0.wireOp",EDGE,"E103"),sQuery(id+"F0.wireOp",EDGE,"E104"),sQuery(id+"F0.wireOp",EDGE,"E107.top"),sQuery(id+"F0.wireOp",EDGE,"E107.right"),sQuery(id+"F0.wireOp",EDGE,"E99.filletArc"),sQuery(id+"F0.wireOp",EDGE,"E98.filletArc"),sQuery(id+"F0.wireOp",EDGE,"E107.left"),sQuery(id+"F0.wireOp",EDGE,"E96.filletArc"),sQuery(id+"F0.wireOp",EDGE,"E97.filletArc"),sQuery(id+"F0.wireOp",EDGE,"E107.bottom"),sQuery(id+"F0.wireOp",EDGE,"E108"),sQuery(id+"F0.wireOp",EDGE,"E109.0.endCap"),sQuery(id+"F0.wireOp",EDGE,"E109.0.startCap"),sQuery(id+"F0.wireOp",EDGE,"E109.0.right"),sQuery(id+"F0.wireOp",EDGE,"E109.0.left"),sQuery(id+"F0.wireOp",EDGE,"E117"),sQuery(id+"F0.wireOp",EDGE,"E118"),sQuery(id+"F0.wireOp",EDGE,"E119"),sQuery(id+"F0.wireOp",EDGE,"E122.top"),sQuery(id+"F0.wireOp",EDGE,"E122.right"),sQuery(id+"F0.wireOp",EDGE,"E114.filletArc"),sQuery(id+"F0.wireOp",EDGE,"E113.filletArc"),sQuery(id+"F0.wireOp",EDGE,"E122.left"),sQuery(id+"F0.wireOp",EDGE,"E111.filletArc"),sQuery(id+"F0.wireOp",EDGE,"E112.filletArc"),sQuery(id+"F0.wireOp",EDGE,"E122.bottom"),sQuery(id+"F0.wireOp",EDGE,"E123"),sQuery(id+"F0.wireOp",EDGE,"E124.0.endCap"),sQuery(id+"F0.wireOp",EDGE,"E124.0.startCap"),sQuery(id+"F0.wireOp",EDGE,"E124.0.right"),sQuery(id+"F0.wireOp",EDGE,"E124.0.left"),sQuery(id+"F0.wireOp",EDGE,"E132"),sQuery(id+"F0.wireOp",EDGE,"E133"),sQuery(id+"F0.wireOp",EDGE,"E134"),sQuery(id+"F0.wireOp",EDGE,"E137.top"),sQuery(id+"F0.wireOp",EDGE,"E137.right"),sQuery(id+"F0.wireOp",EDGE,"E129.filletArc"),sQuery(id+"F0.wireOp",EDGE,"E128.filletArc"),sQuery(id+"F0.wireOp",EDGE,"E137.left"),sQuery(id+"F0.wireOp",EDGE,"E126.filletArc"),sQuery(id+"F0.wireOp",EDGE,"E127.filletArc"),sQuery(id+"F0.wireOp",EDGE,"E137.bottom"),sQuery(id+"F0.wireOp",EDGE,"E138"),sQuery(id+"F0.wireOp",EDGE,"E139.0.endCap"),sQuery(id+"F0.wireOp",EDGE,"E139.0.startCap"),sQuery(id+"F0.wireOp",EDGE,"E139.0.right"),sQuery(id+"F0.wireOp",EDGE,"E139.0.left")])],"isStart":true});
            var sketch = newSketch(context, id + "F18", { "sketchPlane" : qUnion([Q0])});
            skLineSegment(sketch, "E160.bottom", {"start": v(103, 24.7) * mm, "end": v(86, 24.7) * mm});
            skLineSegment(sketch, "E160.top", {"start": v(103, 45.7) * mm, "end": v(86, 45.7) * mm});
            skLineSegment(sketch, "E160.left", {"start": v(105, 26.7) * mm, "end": v(105, 43.7) * mm});
            skLineSegment(sketch, "E160.right", {"start": v(84, 26.7) * mm, "end": v(84, 43.7) * mm});
            skLineSegment(sketch, "E161", {"start": v(94.5, 24.7) * mm, "end": v(94.5, 27.7) * mm, "construction": true});
            skPoint(sketch, "E162.visualSharp", {"position": v(105, 24.7) * mm});
            skArc(sketch, "E162.filletArc", {"start": v(103, 24.7) * mm, "mid": v(104.41, 25.29) * mm, "end": v(105, 26.7) * mm});
            skPoint(sketch, "E163.visualSharp", {"position": v(105, 45.7) * mm});
            skArc(sketch, "E163.filletArc", {"start": v(105, 43.7) * mm, "mid": v(104.41, 45.11) * mm, "end": v(103, 45.7) * mm});
            skPoint(sketch, "E164.visualSharp", {"position": v(84, 45.7) * mm});
            skArc(sketch, "E164.filletArc", {"start": v(86, 45.7) * mm, "mid": v(84.59, 45.11) * mm, "end": v(84, 43.7) * mm});
            skPoint(sketch, "E165.visualSharp", {"position": v(84, 24.7) * mm});
            skArc(sketch, "E165.filletArc", {"start": v(84, 26.7) * mm, "mid": v(84.59, 25.29) * mm, "end": v(86, 24.7) * mm});
            skLineSegment(sketch, "E166.left", {"start": v(78, 14.2) * mm, "end": v(78, 31.2) * mm});
            skLineSegment(sketch, "E166.top", {"start": v(76, 33.2) * mm, "end": v(59, 33.2) * mm});
            skLineSegment(sketch, "E167", {"start": v(67.5, 12.2) * mm, "end": v(67.5, 15.2) * mm, "construction": true});
            skLineSegment(sketch, "E166.right", {"start": v(57, 14.2) * mm, "end": v(57, 31.2) * mm});
            skLineSegment(sketch, "E166.bottom", {"start": v(76, 12.2) * mm, "end": v(59, 12.2) * mm});
            skPoint(sketch, "E168.visualSharp", {"position": v(57, 12.2) * mm});
            skPoint(sketch, "E169.visualSharp", {"position": v(78, 12.2) * mm});
            skPoint(sketch, "E170.visualSharp", {"position": v(78, 33.2) * mm});
            skPoint(sketch, "E171.visualSharp", {"position": v(57, 33.2) * mm});
            skArc(sketch, "E170.filletArc", {"start": v(78, 31.2) * mm, "mid": v(77.41, 32.61) * mm, "end": v(76, 33.2) * mm});
            skArc(sketch, "E169.filletArc", {"start": v(76, 12.2) * mm, "mid": v(77.41, 12.79) * mm, "end": v(78, 14.2) * mm});
            skArc(sketch, "E168.filletArc", {"start": v(57, 14.2) * mm, "mid": v(57.59, 12.79) * mm, "end": v(59, 12.2) * mm});
            skArc(sketch, "E171.filletArc", {"start": v(59, 33.2) * mm, "mid": v(57.59, 32.61) * mm, "end": v(57, 31.2) * mm});
            skLineSegment(sketch, "E172.left", {"start": v(51, 1.7) * mm, "end": v(51, 18.7) * mm});
            skLineSegment(sketch, "E172.top", {"start": v(49, 20.7) * mm, "end": v(32, 20.7) * mm});
            skLineSegment(sketch, "E173", {"start": v(40.5, -0.3) * mm, "end": v(40.5, 2.7) * mm, "construction": true});
            skLineSegment(sketch, "E172.right", {"start": v(30, 1.7) * mm, "end": v(30, 18.7) * mm});
            skLineSegment(sketch, "E172.bottom", {"start": v(49, -0.3) * mm, "end": v(32, -0.3) * mm});
            skPoint(sketch, "E174.visualSharp", {"position": v(30, -0.3) * mm});
            skPoint(sketch, "E175.visualSharp", {"position": v(51, -0.3) * mm});
            skPoint(sketch, "E176.visualSharp", {"position": v(51, 20.7) * mm});
            skPoint(sketch, "E177.visualSharp", {"position": v(30, 20.7) * mm});
            skArc(sketch, "E176.filletArc", {"start": v(51, 18.7) * mm, "mid": v(50.41, 20.11) * mm, "end": v(49, 20.7) * mm});
            skArc(sketch, "E175.filletArc", {"start": v(49, -0.3) * mm, "mid": v(50.41, 0.29) * mm, "end": v(51, 1.7) * mm});
            skArc(sketch, "E174.filletArc", {"start": v(30, 1.7) * mm, "mid": v(30.59, 0.29) * mm, "end": v(32, -0.3) * mm});
            skArc(sketch, "E177.filletArc", {"start": v(32, 20.7) * mm, "mid": v(30.59, 20.11) * mm, "end": v(30, 18.7) * mm});
            skLineSegment(sketch, "E178.left", {"start": v(24, -10.8) * mm, "end": v(24, 6.2) * mm});
            skLineSegment(sketch, "E178.top", {"start": v(22, 8.2) * mm, "end": v(5, 8.2) * mm});
            skLineSegment(sketch, "E179", {"start": v(13.5, -12.8) * mm, "end": v(13.5, -9.8) * mm, "construction": true});
            skLineSegment(sketch, "E178.right", {"start": v(3, -10.8) * mm, "end": v(3, 6.2) * mm});
            skLineSegment(sketch, "E178.bottom", {"start": v(22, -12.8) * mm, "end": v(5, -12.8) * mm});
            skPoint(sketch, "E180.visualSharp", {"position": v(3, -12.8) * mm});
            skPoint(sketch, "E181.visualSharp", {"position": v(24, -12.8) * mm});
            skPoint(sketch, "E182.visualSharp", {"position": v(24, 8.2) * mm});
            skPoint(sketch, "E183.visualSharp", {"position": v(3, 8.2) * mm});
            skArc(sketch, "E182.filletArc", {"start": v(24, 6.2) * mm, "mid": v(23.41, 7.61) * mm, "end": v(22, 8.2) * mm});
            skArc(sketch, "E181.filletArc", {"start": v(22, -12.8) * mm, "mid": v(23.41, -12.21) * mm, "end": v(24, -10.8) * mm});
            skArc(sketch, "E180.filletArc", {"start": v(3, -10.8) * mm, "mid": v(3.59, -12.21) * mm, "end": v(5, -12.8) * mm});
            skArc(sketch, "E183.filletArc", {"start": v(5, 8.2) * mm, "mid": v(3.59, 7.61) * mm, "end": v(3, 6.2) * mm});
            skLineSegment(sketch, "E184.left", {"start": v(-3, -23.3) * mm, "end": v(-3, -6.3) * mm});
            skLineSegment(sketch, "E184.top", {"start": v(-5, -4.3) * mm, "end": v(-22, -4.3) * mm});
            skLineSegment(sketch, "E185", {"start": v(-13.5, -25.3) * mm, "end": v(-13.5, -22.3) * mm, "construction": true});
            skLineSegment(sketch, "E184.right", {"start": v(-24, -23.3) * mm, "end": v(-24, -6.3) * mm});
            skLineSegment(sketch, "E184.bottom", {"start": v(-5, -25.3) * mm, "end": v(-22, -25.3) * mm});
            skPoint(sketch, "E186.visualSharp", {"position": v(-24, -25.3) * mm});
            skPoint(sketch, "E187.visualSharp", {"position": v(-3, -25.3) * mm});
            skPoint(sketch, "E188.visualSharp", {"position": v(-3, -4.3) * mm});
            skPoint(sketch, "E189.visualSharp", {"position": v(-24, -4.3) * mm});
            skArc(sketch, "E188.filletArc", {"start": v(-3, -6.3) * mm, "mid": v(-3.59, -4.89) * mm, "end": v(-5, -4.3) * mm});
            skArc(sketch, "E187.filletArc", {"start": v(-5, -25.3) * mm, "mid": v(-3.59, -24.71) * mm, "end": v(-3, -23.3) * mm});
            skArc(sketch, "E186.filletArc", {"start": v(-24, -23.3) * mm, "mid": v(-23.41, -24.71) * mm, "end": v(-22, -25.3) * mm});
            skArc(sketch, "E189.filletArc", {"start": v(-22, -4.3) * mm, "mid": v(-23.41, -4.89) * mm, "end": v(-24, -6.3) * mm});
            skLineSegment(sketch, "E190.left", {"start": v(-30, -35.8) * mm, "end": v(-30, -18.8) * mm});
            skLineSegment(sketch, "E190.top", {"start": v(-32, -16.8) * mm, "end": v(-49, -16.8) * mm});
            skLineSegment(sketch, "E191", {"start": v(-40.5, -37.8) * mm, "end": v(-40.5, -34.8) * mm, "construction": true});
            skLineSegment(sketch, "E190.right", {"start": v(-51, -35.8) * mm, "end": v(-51, -18.8) * mm});
            skLineSegment(sketch, "E190.bottom", {"start": v(-32, -37.8) * mm, "end": v(-49, -37.8) * mm});
            skPoint(sketch, "E192.visualSharp", {"position": v(-51, -37.8) * mm});
            skPoint(sketch, "E193.visualSharp", {"position": v(-30, -37.8) * mm});
            skPoint(sketch, "E194.visualSharp", {"position": v(-30, -16.8) * mm});
            skPoint(sketch, "E195.visualSharp", {"position": v(-51, -16.8) * mm});
            skArc(sketch, "E194.filletArc", {"start": v(-30, -18.8) * mm, "mid": v(-30.59, -17.39) * mm, "end": v(-32, -16.8) * mm});
            skArc(sketch, "E193.filletArc", {"start": v(-32, -37.8) * mm, "mid": v(-30.59, -37.21) * mm, "end": v(-30, -35.8) * mm});
            skArc(sketch, "E192.filletArc", {"start": v(-51, -35.8) * mm, "mid": v(-50.41, -37.21) * mm, "end": v(-49, -37.8) * mm});
            skArc(sketch, "E195.filletArc", {"start": v(-49, -16.8) * mm, "mid": v(-50.41, -17.39) * mm, "end": v(-51, -18.8) * mm});
            skLineSegment(sketch, "E196.left", {"start": v(-57, -48.3) * mm, "end": v(-57, -31.3) * mm});
            skLineSegment(sketch, "E196.top", {"start": v(-59, -29.3) * mm, "end": v(-76, -29.3) * mm});
            skLineSegment(sketch, "E197", {"start": v(-67.5, -50.3) * mm, "end": v(-67.5, -47.3) * mm, "construction": true});
            skLineSegment(sketch, "E196.right", {"start": v(-78, -48.3) * mm, "end": v(-78, -31.3) * mm});
            skLineSegment(sketch, "E196.bottom", {"start": v(-59, -50.3) * mm, "end": v(-76, -50.3) * mm});
            skPoint(sketch, "E198.visualSharp", {"position": v(-78, -50.3) * mm});
            skPoint(sketch, "E199.visualSharp", {"position": v(-57, -50.3) * mm});
            skPoint(sketch, "E200.visualSharp", {"position": v(-57, -29.3) * mm});
            skPoint(sketch, "E201.visualSharp", {"position": v(-78, -29.3) * mm});
            skArc(sketch, "E200.filletArc", {"start": v(-57, -31.3) * mm, "mid": v(-57.59, -29.89) * mm, "end": v(-59, -29.3) * mm});
            skArc(sketch, "E199.filletArc", {"start": v(-59, -50.3) * mm, "mid": v(-57.59, -49.71) * mm, "end": v(-57, -48.3) * mm});
            skArc(sketch, "E198.filletArc", {"start": v(-78, -48.3) * mm, "mid": v(-77.41, -49.71) * mm, "end": v(-76, -50.3) * mm});
            skArc(sketch, "E201.filletArc", {"start": v(-76, -29.3) * mm, "mid": v(-77.41, -29.89) * mm, "end": v(-78, -31.3) * mm});
            skLineSegment(sketch, "E202.left", {"start": v(-84, -60.8) * mm, "end": v(-84, -43.8) * mm});
            skLineSegment(sketch, "E202.top", {"start": v(-86, -41.8) * mm, "end": v(-103, -41.8) * mm});
            skLineSegment(sketch, "E203", {"start": v(-94.5, -62.8) * mm, "end": v(-94.5, -59.8) * mm, "construction": true});
            skLineSegment(sketch, "E202.right", {"start": v(-105, -60.8) * mm, "end": v(-105, -43.8) * mm});
            skLineSegment(sketch, "E202.bottom", {"start": v(-86, -62.8) * mm, "end": v(-103, -62.8) * mm});
            skPoint(sketch, "E204.visualSharp", {"position": v(-105, -62.8) * mm});
            skPoint(sketch, "E205.visualSharp", {"position": v(-84, -62.8) * mm});
            skPoint(sketch, "E206.visualSharp", {"position": v(-84, -41.8) * mm});
            skPoint(sketch, "E207.visualSharp", {"position": v(-105, -41.8) * mm});
            skArc(sketch, "E206.filletArc", {"start": v(-84, -43.8) * mm, "mid": v(-84.59, -42.39) * mm, "end": v(-86, -41.8) * mm});
            skArc(sketch, "E205.filletArc", {"start": v(-86, -62.8) * mm, "mid": v(-84.59, -62.21) * mm, "end": v(-84, -60.8) * mm});
            skArc(sketch, "E204.filletArc", {"start": v(-105, -60.8) * mm, "mid": v(-104.41, -62.21) * mm, "end": v(-103, -62.8) * mm});
            skArc(sketch, "E207.filletArc", {"start": v(-103, -41.8) * mm, "mid": v(-104.41, -42.39) * mm, "end": v(-105, -43.8) * mm});
            skSolve(sketch);
        }
        {
            var Q0;
            Q0 = qSketchRegion(id + "F18", true);
            extrude(context, id + "F19", {"entities" : qUnion([Q0]), "operationType" : NewBodyOperationType.REMOVE, "oppositeDirection" : true, "depth" : 7 * mm});
        }
        {
            var Q0;
            Q0=makeQuery(id+"F1.opExtrude","CAP_FACE",FACE,{"disambiguationData":[OSD([sQuery(id+"F0.wireOp",EDGE,"E20.bottom"),sQuery(id+"F0.wireOp",EDGE,"E20.top"),sQuery(id+"F0.wireOp",EDGE,"E20.left"),sQuery(id+"F0.wireOp",EDGE,"E20.right"),sQuery(id+"F0.wireOp",EDGE,"E24.bottom"),sQuery(id+"F0.wireOp",EDGE,"E24.top"),sQuery(id+"F0.wireOp",EDGE,"E24.left"),sQuery(id+"F0.wireOp",EDGE,"E24.right"),sQuery(id+"F0.wireOp",EDGE,"E25.filletArc"),sQuery(id+"F0.wireOp",EDGE,"E26.filletArc"),sQuery(id+"F0.wireOp",EDGE,"E27.filletArc"),sQuery(id+"F0.wireOp",EDGE,"E28.filletArc"),sQuery(id+"F0.wireOp",EDGE,"E31.0.startCap"),sQuery(id+"F0.wireOp",EDGE,"E31.0.endCap"),sQuery(id+"F0.wireOp",EDGE,"E31.0.left"),sQuery(id+"F0.wireOp",EDGE,"E31.0.right"),sQuery(id+"F0.wireOp",EDGE,"E32"),sQuery(id+"F0.wireOp",EDGE,"E33"),sQuery(id+"F0.wireOp",EDGE,"E34"),sQuery(id+"F0.wireOp",EDGE,"E35"),sQuery(id+"F0.wireOp",EDGE,"E42"),sQuery(id+"F0.wireOp",EDGE,"E43"),sQuery(id+"F0.wireOp",EDGE,"E44"),sQuery(id+"F0.wireOp",EDGE,"E47.top"),sQuery(id+"F0.wireOp",EDGE,"E47.right"),sQuery(id+"F0.wireOp",EDGE,"E39.filletArc"),sQuery(id+"F0.wireOp",EDGE,"E38.filletArc"),sQuery(id+"F0.wireOp",EDGE,"E47.left"),sQuery(id+"F0.wireOp",EDGE,"E36.filletArc"),sQuery(id+"F0.wireOp",EDGE,"E37.filletArc"),sQuery(id+"F0.wireOp",EDGE,"E47.bottom"),sQuery(id+"F0.wireOp",EDGE,"E48"),sQuery(id+"F0.wireOp",EDGE,"E49.0.endCap"),sQuery(id+"F0.wireOp",EDGE,"E49.0.startCap"),sQuery(id+"F0.wireOp",EDGE,"E49.0.right"),sQuery(id+"F0.wireOp",EDGE,"E49.0.left"),sQuery(id+"F0.wireOp",EDGE,"E57"),sQuery(id+"F0.wireOp",EDGE,"E58"),sQuery(id+"F0.wireOp",EDGE,"E59"),sQuery(id+"F0.wireOp",EDGE,"E62.top"),sQuery(id+"F0.wireOp",EDGE,"E62.right"),sQuery(id+"F0.wireOp",EDGE,"E54.filletArc"),sQuery(id+"F0.wireOp",EDGE,"E53.filletArc"),sQuery(id+"F0.wireOp",EDGE,"E62.left"),sQuery(id+"F0.wireOp",EDGE,"E51.filletArc"),sQuery(id+"F0.wireOp",EDGE,"E52.filletArc"),sQuery(id+"F0.wireOp",EDGE,"E62.bottom"),sQuery(id+"F0.wireOp",EDGE,"E63"),sQuery(id+"F0.wireOp",EDGE,"E64.0.endCap"),sQuery(id+"F0.wireOp",EDGE,"E64.0.startCap"),sQuery(id+"F0.wireOp",EDGE,"E64.0.right"),sQuery(id+"F0.wireOp",EDGE,"E64.0.left"),sQuery(id+"F0.wireOp",EDGE,"E72"),sQuery(id+"F0.wireOp",EDGE,"E73"),sQuery(id+"F0.wireOp",EDGE,"E74"),sQuery(id+"F0.wireOp",EDGE,"E77.top"),sQuery(id+"F0.wireOp",EDGE,"E77.right"),sQuery(id+"F0.wireOp",EDGE,"E69.filletArc"),sQuery(id+"F0.wireOp",EDGE,"E68.filletArc"),sQuery(id+"F0.wireOp",EDGE,"E77.left"),sQuery(id+"F0.wireOp",EDGE,"E66.filletArc"),sQuery(id+"F0.wireOp",EDGE,"E67.filletArc"),sQuery(id+"F0.wireOp",EDGE,"E77.bottom"),sQuery(id+"F0.wireOp",EDGE,"E78"),sQuery(id+"F0.wireOp",EDGE,"E79.0.endCap"),sQuery(id+"F0.wireOp",EDGE,"E79.0.startCap"),sQuery(id+"F0.wireOp",EDGE,"E79.0.right"),sQuery(id+"F0.wireOp",EDGE,"E79.0.left"),sQuery(id+"F0.wireOp",EDGE,"E87"),sQuery(id+"F0.wireOp",EDGE,"E88"),sQuery(id+"F0.wireOp",EDGE,"E89"),sQuery(id+"F0.wireOp",EDGE,"E92.top"),sQuery(id+"F0.wireOp",EDGE,"E92.right"),sQuery(id+"F0.wireOp",EDGE,"E84.filletArc"),sQuery(id+"F0.wireOp",EDGE,"E83.filletArc"),sQuery(id+"F0.wireOp",EDGE,"E92.left"),sQuery(id+"F0.wireOp",EDGE,"E81.filletArc"),sQuery(id+"F0.wireOp",EDGE,"E82.filletArc"),sQuery(id+"F0.wireOp",EDGE,"E92.bottom"),sQuery(id+"F0.wireOp",EDGE,"E93"),sQuery(id+"F0.wireOp",EDGE,"E94.0.endCap"),sQuery(id+"F0.wireOp",EDGE,"E94.0.startCap"),sQuery(id+"F0.wireOp",EDGE,"E94.0.right"),sQuery(id+"F0.wireOp",EDGE,"E94.0.left"),sQuery(id+"F0.wireOp",EDGE,"E102"),sQuery(id+"F0.wireOp",EDGE,"E103"),sQuery(id+"F0.wireOp",EDGE,"E104"),sQuery(id+"F0.wireOp",EDGE,"E107.top"),sQuery(id+"F0.wireOp",EDGE,"E107.right"),sQuery(id+"F0.wireOp",EDGE,"E99.filletArc"),sQuery(id+"F0.wireOp",EDGE,"E98.filletArc"),sQuery(id+"F0.wireOp",EDGE,"E107.left"),sQuery(id+"F0.wireOp",EDGE,"E96.filletArc"),sQuery(id+"F0.wireOp",EDGE,"E97.filletArc"),sQuery(id+"F0.wireOp",EDGE,"E107.bottom"),sQuery(id+"F0.wireOp",EDGE,"E108"),sQuery(id+"F0.wireOp",EDGE,"E109.0.endCap"),sQuery(id+"F0.wireOp",EDGE,"E109.0.startCap"),sQuery(id+"F0.wireOp",EDGE,"E109.0.right"),sQuery(id+"F0.wireOp",EDGE,"E109.0.left"),sQuery(id+"F0.wireOp",EDGE,"E117"),sQuery(id+"F0.wireOp",EDGE,"E118"),sQuery(id+"F0.wireOp",EDGE,"E119"),sQuery(id+"F0.wireOp",EDGE,"E122.top"),sQuery(id+"F0.wireOp",EDGE,"E122.right"),sQuery(id+"F0.wireOp",EDGE,"E114.filletArc"),sQuery(id+"F0.wireOp",EDGE,"E113.filletArc"),sQuery(id+"F0.wireOp",EDGE,"E122.left"),sQuery(id+"F0.wireOp",EDGE,"E111.filletArc"),sQuery(id+"F0.wireOp",EDGE,"E112.filletArc"),sQuery(id+"F0.wireOp",EDGE,"E122.bottom"),sQuery(id+"F0.wireOp",EDGE,"E123"),sQuery(id+"F0.wireOp",EDGE,"E124.0.endCap"),sQuery(id+"F0.wireOp",EDGE,"E124.0.startCap"),sQuery(id+"F0.wireOp",EDGE,"E124.0.right"),sQuery(id+"F0.wireOp",EDGE,"E124.0.left"),sQuery(id+"F0.wireOp",EDGE,"E132"),sQuery(id+"F0.wireOp",EDGE,"E133"),sQuery(id+"F0.wireOp",EDGE,"E134"),sQuery(id+"F0.wireOp",EDGE,"E137.top"),sQuery(id+"F0.wireOp",EDGE,"E137.right"),sQuery(id+"F0.wireOp",EDGE,"E129.filletArc"),sQuery(id+"F0.wireOp",EDGE,"E128.filletArc"),sQuery(id+"F0.wireOp",EDGE,"E137.left"),sQuery(id+"F0.wireOp",EDGE,"E126.filletArc"),sQuery(id+"F0.wireOp",EDGE,"E127.filletArc"),sQuery(id+"F0.wireOp",EDGE,"E137.bottom"),sQuery(id+"F0.wireOp",EDGE,"E138"),sQuery(id+"F0.wireOp",EDGE,"E139.0.endCap"),sQuery(id+"F0.wireOp",EDGE,"E139.0.startCap"),sQuery(id+"F0.wireOp",EDGE,"E139.0.right"),sQuery(id+"F0.wireOp",EDGE,"E139.0.left")])],"isStart":true});
            var sketch = newSketch(context, id + "F20", { "sketchPlane" : qUnion([Q0])});
            skLineSegment(sketch, "E208", {"start": v(105, 26.7) * mm, "end": v(105, 19.7) * mm});
            skLineSegment(sketch, "E209", {"start": v(84, 26.7) * mm, "end": v(84, 19.7) * mm});
            skLineSegment(sketch, "E210", {"start": v(101, 19.7) * mm, "end": v(88, 19.7) * mm});
            skArc(sketch, "E211", {"start": v(101, 19.7) * mm, "mid": v(103, 17.7) * mm, "end": v(105, 19.7) * mm});
            skArc(sketch, "E212", {"start": v(84, 19.7) * mm, "mid": v(86, 17.7) * mm, "end": v(88, 19.7) * mm});
            skLineSegment(sketch, "E213", {"start": v(105, 26.7) * mm, "end": v(84, 26.7) * mm});
            skArc(sketch, "E214", {"start": v(74, 7.3) * mm, "mid": v(76, 5.3) * mm, "end": v(78, 7.3) * mm});
            skLineSegment(sketch, "E215", {"start": v(78, 14.2) * mm, "end": v(78, 7.3) * mm});
            skLineSegment(sketch, "E216", {"start": v(57, 14.2) * mm, "end": v(57, 7.3) * mm});
            skArc(sketch, "E217", {"start": v(57, 7.3) * mm, "mid": v(59, 5.3) * mm, "end": v(61, 7.3) * mm});
            skLineSegment(sketch, "E218", {"start": v(78, 14.2) * mm, "end": v(57, 14.2) * mm});
            skLineSegment(sketch, "E219", {"start": v(74, 7.3) * mm, "end": v(61, 7.3) * mm});
            skLineSegment(sketch, "E220", {"start": v(51, 1.7) * mm, "end": v(30, 1.7) * mm});
            skArc(sketch, "E221", {"start": v(30, -5.1) * mm, "mid": v(32, -7.1) * mm, "end": v(34, -5.1) * mm});
            skArc(sketch, "E222", {"start": v(47, -5.1) * mm, "mid": v(49, -7.1) * mm, "end": v(51, -5.1) * mm});
            skLineSegment(sketch, "E223", {"start": v(51, 1.7) * mm, "end": v(51, -5.1) * mm});
            skLineSegment(sketch, "E224", {"start": v(30, 1.7) * mm, "end": v(30, -5.1) * mm});
            skLineSegment(sketch, "E225", {"start": v(47, -5.1) * mm, "end": v(34, -5.1) * mm});
            skLineSegment(sketch, "E226", {"start": v(24, -10.8) * mm, "end": v(3, -10.8) * mm});
            skArc(sketch, "E227", {"start": v(3, -17.5) * mm, "mid": v(5, -19.5) * mm, "end": v(7, -17.5) * mm});
            skArc(sketch, "E228", {"start": v(20, -17.5) * mm, "mid": v(22, -19.5) * mm, "end": v(24, -17.5) * mm});
            skLineSegment(sketch, "E229", {"start": v(24, -10.8) * mm, "end": v(24, -17.5) * mm});
            skLineSegment(sketch, "E230", {"start": v(3, -10.8) * mm, "end": v(3, -17.5) * mm});
            skLineSegment(sketch, "E231", {"start": v(20, -17.5) * mm, "end": v(7, -17.5) * mm});
            skLineSegment(sketch, "E232", {"start": v(-3, -23.3) * mm, "end": v(-24, -23.3) * mm});
            skArc(sketch, "E233", {"start": v(-24, -29.9) * mm, "mid": v(-22, -31.9) * mm, "end": v(-20, -29.9) * mm});
            skArc(sketch, "E234", {"start": v(-7, -29.9) * mm, "mid": v(-5, -31.9) * mm, "end": v(-3, -29.9) * mm});
            skLineSegment(sketch, "E235", {"start": v(-3, -23.3) * mm, "end": v(-3, -29.9) * mm});
            skLineSegment(sketch, "E236", {"start": v(-24, -23.3) * mm, "end": v(-24, -29.9) * mm});
            skLineSegment(sketch, "E237", {"start": v(-7, -29.9) * mm, "end": v(-20, -29.9) * mm});
            skLineSegment(sketch, "E238", {"start": v(-30, -35.8) * mm, "end": v(-51, -35.8) * mm});
            skArc(sketch, "E239", {"start": v(-51, -42.3) * mm, "mid": v(-49, -44.3) * mm, "end": v(-47, -42.3) * mm});
            skArc(sketch, "E240", {"start": v(-34, -42.3) * mm, "mid": v(-32, -44.3) * mm, "end": v(-30, -42.3) * mm});
            skLineSegment(sketch, "E241", {"start": v(-30, -35.8) * mm, "end": v(-30, -42.3) * mm});
            skLineSegment(sketch, "E242", {"start": v(-51, -35.8) * mm, "end": v(-51, -42.3) * mm});
            skLineSegment(sketch, "E243", {"start": v(-34, -42.3) * mm, "end": v(-47, -42.3) * mm});
            skLineSegment(sketch, "E244", {"start": v(-57, -48.3) * mm, "end": v(-78, -48.3) * mm});
            skArc(sketch, "E245", {"start": v(-78, -54.7) * mm, "mid": v(-76, -56.7) * mm, "end": v(-74, -54.7) * mm});
            skArc(sketch, "E246", {"start": v(-61, -54.7) * mm, "mid": v(-59, -56.7) * mm, "end": v(-57, -54.7) * mm});
            skLineSegment(sketch, "E247", {"start": v(-57, -48.3) * mm, "end": v(-57, -54.7) * mm});
            skLineSegment(sketch, "E248", {"start": v(-78, -48.3) * mm, "end": v(-78, -54.7) * mm});
            skLineSegment(sketch, "E249", {"start": v(-61, -54.7) * mm, "end": v(-74, -54.7) * mm});
            skLineSegment(sketch, "E250", {"start": v(-84, -60.8) * mm, "end": v(-105, -60.8) * mm});
            skArc(sketch, "E251", {"start": v(-105, -67.1) * mm, "mid": v(-103, -69.1) * mm, "end": v(-101, -67.1) * mm});
            skArc(sketch, "E252", {"start": v(-88, -67.1) * mm, "mid": v(-86, -69.1) * mm, "end": v(-84, -67.1) * mm});
            skLineSegment(sketch, "E253", {"start": v(-84, -60.8) * mm, "end": v(-84, -67.1) * mm});
            skLineSegment(sketch, "E254", {"start": v(-88, -67.1) * mm, "end": v(-101, -67.1) * mm});
            skLineSegment(sketch, "E255", {"start": v(-105, -60.8) * mm, "end": v(-105, -67.1) * mm});
            skSolve(sketch);
        }
        {
            var Q0;
            Q0 = qSketchRegion(id + "F20", true);
            extrude(context, id + "F21", {"entities" : qUnion([Q0]), "operationType" : NewBodyOperationType.REMOVE, "oppositeDirection" : true, "depth" : 5 * mm});
        }
        {
            var Q0;
            Q0=makeQuery(id+"F11.opExtrude","CAP_FACE",FACE,{"disambiguationData":[OSD([sQuery(id+"F10.wireOp",EDGE,"E149.bottom"),sQuery(id+"F10.wireOp",EDGE,"E149.top"),sQuery(id+"F10.wireOp",EDGE,"E149.left"),sQuery(id+"F10.wireOp",EDGE,"E149.right")])],"isStart":true});
            var sketch = newSketch(context, id + "F22", { "sketchPlane" : qUnion([Q0])});
            skLineSegment(sketch, "E256.top", {"start": v(-102.5, -10) * mm, "end": v(-2.5, -10) * mm, "construction": true});
            skLineSegment(sketch, "E256.left", {"start": v(-102.5, 50) * mm, "end": v(-102.5, -10) * mm, "construction": true});
            skLineSegment(sketch, "E257", {"start": v(-99.5, 20) * mm, "end": v(-99.5, -6) * mm, "construction": true});
            skLineSegment(sketch, "E258", {"start": v(-5.5, 16) * mm, "end": v(-5.5, -6) * mm, "construction": true});
            skLineSegment(sketch, "E259", {"start": v(-99.5, -6) * mm, "end": v(-5.5, -6) * mm, "construction": true});
            skCircle(sketch, "E260", {"center": v(-99.5, 20) * mm, "radius": 1.75 * mm});
            skCircle(sketch, "E261", {"center": v(-5.5, 16) * mm, "radius": 1.75 * mm});
            skCircle(sketch, "E262", {"center": v(-99.5, -6) * mm, "radius": 1.75 * mm});
            skCircle(sketch, "E263", {"center": v(-5.5, -6) * mm, "radius": 1.75 * mm});
            skLineSegment(sketch, "E256.bottom", {"start": v(-102.5, 50) * mm, "end": v(-2.5, 50) * mm, "construction": true});
            skLineSegment(sketch, "E256.right", {"start": v(-2.5, 50) * mm, "end": v(-2.5, -10) * mm, "construction": true});
            skLineSegment(sketch, "E264.top", {"start": v(2.5, -60) * mm, "end": v(102.5, -60) * mm, "construction": true});
            skLineSegment(sketch, "E264.left", {"start": v(2.5, 0) * mm, "end": v(2.5, -60) * mm, "construction": true});
            skLineSegment(sketch, "E265", {"start": v(5.5, -30) * mm, "end": v(5.5, -56) * mm, "construction": true});
            skLineSegment(sketch, "E266", {"start": v(99.5, -34) * mm, "end": v(99.5, -56) * mm, "construction": true});
            skLineSegment(sketch, "E267", {"start": v(5.5, -56) * mm, "end": v(99.5, -56) * mm, "construction": true});
            skCircle(sketch, "E268", {"center": v(5.5, -30) * mm, "radius": 1.75 * mm});
            skCircle(sketch, "E269", {"center": v(99.5, -34) * mm, "radius": 1.75 * mm});
            skCircle(sketch, "E270", {"center": v(5.5, -56) * mm, "radius": 1.75 * mm});
            skCircle(sketch, "E271", {"center": v(99.5, -56) * mm, "radius": 1.75 * mm});
            skLineSegment(sketch, "E264.bottom", {"start": v(2.5, 0) * mm, "end": v(102.5, 0) * mm, "construction": true});
            skLineSegment(sketch, "E264.right", {"start": v(102.5, 0) * mm, "end": v(102.5, -60) * mm, "construction": true});
            skLineSegment(sketch, "E272", {"start": v(-102.5, 50) * mm, "end": v(-125, 50) * mm, "construction": true});
            skLineSegment(sketch, "E273", {"start": v(102.5, 0) * mm, "end": v(125, 0) * mm, "construction": true});
            skSolve(sketch);
        }
        {
            var Q0;
            Q0 = qSketchRegion(id + "F22", true);
            extrude(context, id + "F23", {"entities" : qUnion([Q0]), "operationType" : NewBodyOperationType.REMOVE, "endBound" : BoundingType.THROUGH_ALL, "oppositeDirection" : true, "depth" : 25 * mm});
        }
        {
            var Q0;
            Q0=makeQuery(id+"F1.opExtrude","CAP_EDGE",EDGE,{"disambiguationData":[OSD([sQuery(id+"F0.wireOp",EDGE,"E20.bottom")])],"isStart":false});
            var Q1;
            Q1=makeQuery(id+"F1.opExtrude","CAP_EDGE",EDGE,{"disambiguationData":[OSD([sQuery(id+"F0.wireOp",EDGE,"E20.left")])],"isStart":false});
            var Q2;
            Q2=makeQuery(id+"F1.opExtrude","SWEPT_EDGE",EDGE,{"disambiguationData":[OSD([sQuery(id+"F0.wireOp",EDGE,"E20.bottom"),sQuery(id+"F0.wireOp",EDGE,"E20.left")])]});
            var Q3;
            Q3=makeQuery(id+"F1.opExtrude","CAP_EDGE",EDGE,{"disambiguationData":[OSD([sQuery(id+"F0.wireOp",EDGE,"E20.bottom")])],"isStart":true});
            var Q4;
            Q4=makeQuery(id+"F1.opExtrude","CAP_EDGE",EDGE,{"disambiguationData":[OSD([sQuery(id+"F0.wireOp",EDGE,"E20.left")])],"isStart":true});
            var Q5;
            Q5=makeQuery(id+"F1.opExtrude","SWEPT_EDGE",EDGE,{"disambiguationData":[OSD([sQuery(id+"F0.wireOp",EDGE,"E20.top"),sQuery(id+"F0.wireOp",EDGE,"E20.right")])]});
            var Q6;
            Q6=makeQuery(id+"F1.opExtrude","CAP_EDGE",EDGE,{"disambiguationData":[OSD([sQuery(id+"F0.wireOp",EDGE,"E20.right")])],"isStart":false});
            var Q7;
            Q7=makeQuery(id+"F1.opExtrude","CAP_EDGE",EDGE,{"disambiguationData":[OSD([sQuery(id+"F0.wireOp",EDGE,"E20.top")])],"isStart":false});
            var Q8;
            Q8=makeQuery(id+"F1.opExtrude","CAP_EDGE",EDGE,{"disambiguationData":[OSD([sQuery(id+"F0.wireOp",EDGE,"E20.right")])],"isStart":true});
            var Q9;
            Q9=makeQuery(id+"F1.opExtrude","SWEPT_EDGE",EDGE,{"disambiguationData":[OSD([sQuery(id+"F0.wireOp",EDGE,"E20.bottom"),sQuery(id+"F0.wireOp",EDGE,"E20.right")])]});
            var Q10;
            Q10=makeQuery(id+"F1.opExtrude","SWEPT_EDGE",EDGE,{"disambiguationData":[OSD([sQuery(id+"F0.wireOp",EDGE,"E20.top"),sQuery(id+"F0.wireOp",EDGE,"E20.left")])]});
            var Q11;
            Q11=makeQuery(id+"F1.opExtrude","CAP_EDGE",EDGE,{"disambiguationData":[OSD([sQuery(id+"F0.wireOp",EDGE,"E20.top")])],"isStart":true});
            chamfer(context, id + "F24", {"entities" : qUnion([Q0, Q1, Q2, Q3, Q4, Q5, Q6, Q7, Q8, Q9, Q10, Q11]), "width" : 1 * mm, "tangentPropagation" : true});
        }
        {
            var Q0;
            Q0=makeQuery(id+"F11.opExtrude","SWEPT_EDGE",EDGE,{"disambiguationData":[OSD([sQuery(id+"F10.wireOp",EDGE,"E149.top"),sQuery(id+"F10.wireOp",EDGE,"E149.left")])]});
            var Q1;
            Q1=makeQuery(id+"F9.opShell","OFFSET_EDGE",EDGE,{"disambiguationData":[OSD([sQuery(id+"F2.wireOp",EDGE,"E144.bottom"),sQuery(id+"F2.wireOp",EDGE,"E144.left"),sQuery(id+"F4.wireOp",EDGE,"E148.bottom"),sQuery(id+"F4.wireOp",EDGE,"E148.left")])]});
            var Q2;
            Q2=makeQuery(id+"F11.opExtrude","SWEPT_EDGE",EDGE,{"disambiguationData":[OSD([sQuery(id+"F10.wireOp",EDGE,"E149.top"),sQuery(id+"F10.wireOp",EDGE,"E149.right")])]});
            var Q3;
            Q3=makeQuery(id+"F9.opShell","OFFSET_EDGE",EDGE,{"disambiguationData":[OSD([sQuery(id+"F2.wireOp",EDGE,"E143.bottom"),sQuery(id+"F2.wireOp",EDGE,"E143.left"),sQuery(id+"F4.wireOp",EDGE,"E147.bottom"),sQuery(id+"F4.wireOp",EDGE,"E147.left")])]});
            var Q4;
            Q4=makeQuery(id+"F11.opExtrude","SWEPT_EDGE",EDGE,{"disambiguationData":[OSD([sQuery(id+"F10.wireOp",EDGE,"E149.bottom"),sQuery(id+"F10.wireOp",EDGE,"E149.right")])]});
            var Q5;
            Q5=makeQuery(id+"F9.opShell","OFFSET_EDGE",EDGE,{"disambiguationData":[OSD([sQuery(id+"F2.wireOp",EDGE,"E142.bottom"),sQuery(id+"F2.wireOp",EDGE,"E142.left"),sQuery(id+"F4.wireOp",EDGE,"E146.bottom"),sQuery(id+"F4.wireOp",EDGE,"E146.left")])]});
            var Q6;
            Q6=makeQuery(id+"F9.opShell","OFFSET_EDGE",EDGE,{"disambiguationData":[OSD([sQuery(id+"F2.wireOp",EDGE,"E141.bottom"),sQuery(id+"F2.wireOp",EDGE,"E141.left"),sQuery(id+"F4.wireOp",EDGE,"E145.bottom"),sQuery(id+"F4.wireOp",EDGE,"E145.left")])]});
            var Q7;
            Q7=makeQuery(id+"F11.opExtrude","SWEPT_EDGE",EDGE,{"disambiguationData":[OSD([sQuery(id+"F10.wireOp",EDGE,"E149.bottom"),sQuery(id+"F10.wireOp",EDGE,"E149.left")])]});
            var Q8;
            Q8=makeQuery(id+"F8.opLoft","SWEPT_EDGE",EDGE,{"disambiguationData":[OSD([sQuery(id+"F2.wireOp",EDGE,"E143.bottom"),sQuery(id+"F2.wireOp",EDGE,"E143.left"),sQuery(id+"F4.wireOp",EDGE,"E147.bottom"),sQuery(id+"F4.wireOp",EDGE,"E147.left")])]});
            var Q9;
            Q9=makeQuery(id+"F7.opLoft","SWEPT_EDGE",EDGE,{"disambiguationData":[OSD([sQuery(id+"F2.wireOp",EDGE,"E144.bottom"),sQuery(id+"F2.wireOp",EDGE,"E144.left"),sQuery(id+"F4.wireOp",EDGE,"E148.bottom"),sQuery(id+"F4.wireOp",EDGE,"E148.left")])]});
            var Q10;
            Q10=makeQuery(id+"F5.opLoft","SWEPT_EDGE",EDGE,{"disambiguationData":[OSD([sQuery(id+"F2.wireOp",EDGE,"E141.bottom"),sQuery(id+"F2.wireOp",EDGE,"E141.left"),sQuery(id+"F4.wireOp",EDGE,"E145.bottom"),sQuery(id+"F4.wireOp",EDGE,"E145.left")])]});
            var Q11;
            Q11=makeQuery(id+"F6.opLoft","SWEPT_EDGE",EDGE,{"disambiguationData":[OSD([sQuery(id+"F2.wireOp",EDGE,"E142.bottom"),sQuery(id+"F2.wireOp",EDGE,"E142.left"),sQuery(id+"F4.wireOp",EDGE,"E146.bottom"),sQuery(id+"F4.wireOp",EDGE,"E146.left")])]});
            fillet(context, id + "F25", {"entities" : qUnion([Q0, Q1, Q2, Q3, Q4, Q5, Q6, Q7, Q8, Q9, Q10, Q11]), "radius" : 2 * mm, "tangentPropagation" : true, "allowEdgeOverflow" : false});
        }
    });
